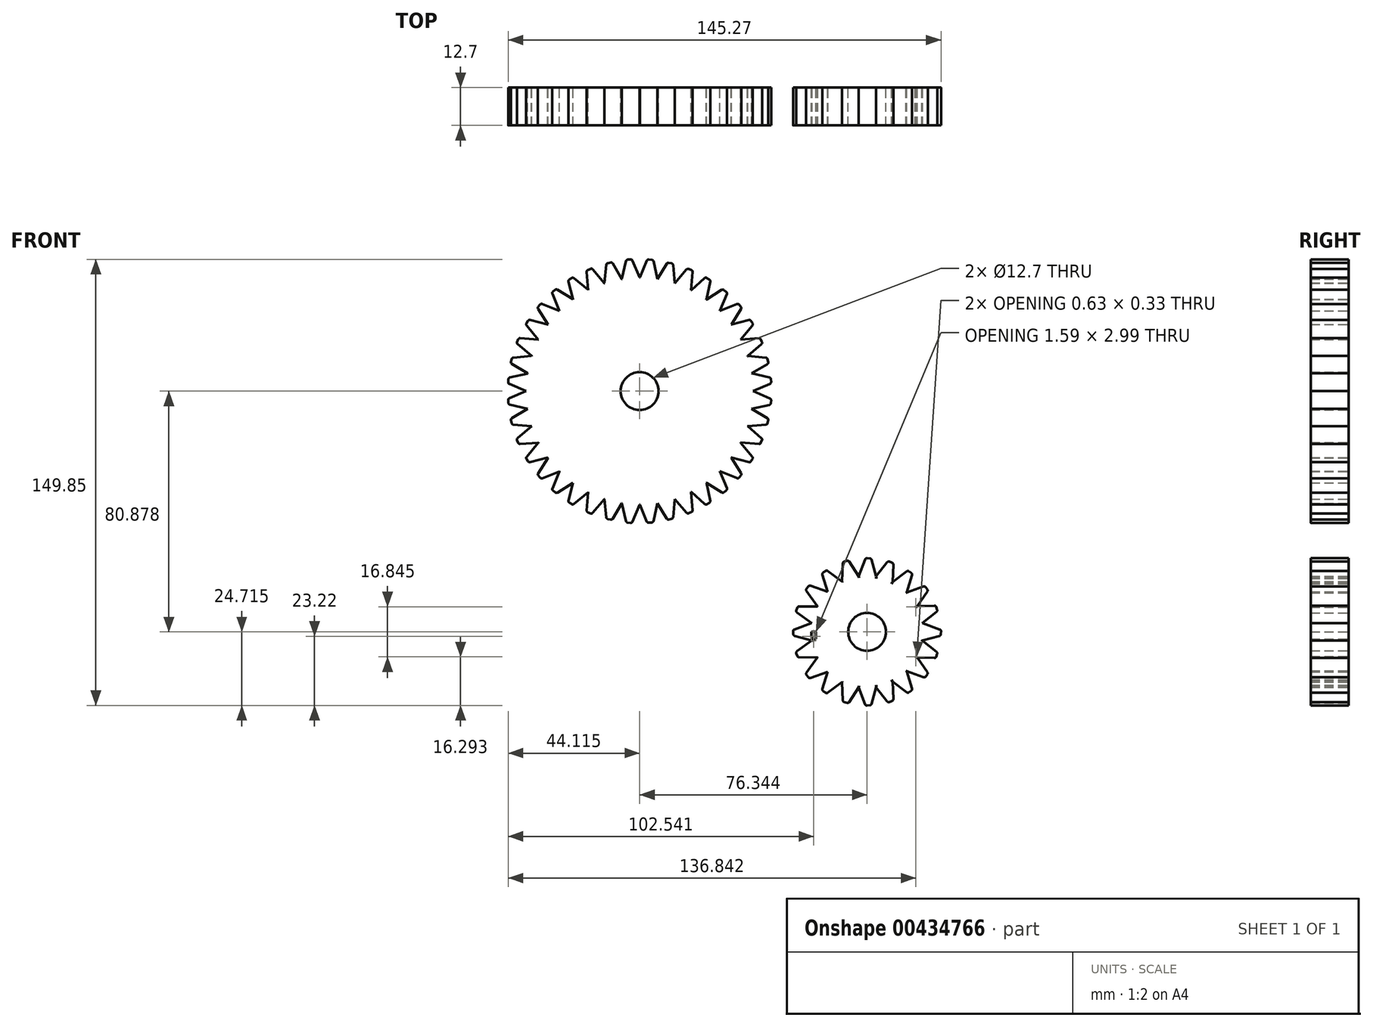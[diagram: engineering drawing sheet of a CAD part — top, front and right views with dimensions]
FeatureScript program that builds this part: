
annotation { "Feature Type Name" : "Feature", "Feature Type Description" : "" }
export const myFeature = defineFeature(function(context is Context, id is Id, definition is map)
    precondition{}
    {
        {
            var Q0;
            Q0=qCreatedBy(makeId("Front.planeOp"),FACE);
            var sketch = newSketch(context, id + "F0", { "sketchPlane" : qUnion([Q0])});
            skCircle(sketch, "E0", {"center": v(-35.87, 35.66) * mm, "radius": 38.1 * mm});
            skCircle(sketch, "E1", {"center": v(40.47, -45.22) * mm, "radius": 18.71 * mm});
            skCircle(sketch, "E2", {"center": v(-35.87, 35.66) * mm, "radius": 6.35 * mm});
            skCircle(sketch, "E3", {"center": v(40.47, -45.22) * mm, "radius": 6.35 * mm});
            skLineSegment(sketch, "E4", {"start": v(2.23, 35.66) * mm, "end": v(-73.97, 35.66) * mm, "construction": true});
            skLineSegment(sketch, "E5", {"start": v(-35.87, 73.76) * mm, "end": v(-35.87, -2.44) * mm, "construction": true});
            skLineSegment(sketch, "E6", {"start": v(-35.87, 35.66) * mm, "end": v(-41.83, 73.3) * mm, "construction": true});
            skLineSegment(sketch, "E7", {"start": v(-35.87, 35.66) * mm, "end": v(-47.65, 71.9) * mm, "construction": true});
            skLineSegment(sketch, "E8", {"start": v(-35.87, 35.66) * mm, "end": v(-53.17, 69.61) * mm, "construction": true});
            skLineSegment(sketch, "E9", {"start": v(-35.87, 35.66) * mm, "end": v(-58.27, 66.49) * mm, "construction": true});
            skLineSegment(sketch, "E10", {"start": v(-35.87, 35.66) * mm, "end": v(-62.82, 62.6) * mm, "construction": true});
            skLineSegment(sketch, "E11", {"start": v(-35.87, 35.66) * mm, "end": v(-66.7, 58.06) * mm, "construction": true});
            skLineSegment(sketch, "E12", {"start": v(-35.87, 35.66) * mm, "end": v(-69.82, 52.96) * mm, "construction": true});
            skLineSegment(sketch, "E13", {"start": v(-35.87, 35.66) * mm, "end": v(-72.1, 47.44) * mm, "construction": true});
            skLineSegment(sketch, "E14", {"start": v(-35.87, 35.66) * mm, "end": v(-73.5, 41.62) * mm, "construction": true});
            skLineSegment(sketch, "E15.MirrorCS", {"start": v(-35.87, 35.66) * mm, "end": v(1.76, 29.7) * mm, "construction": true});
            skLineSegment(sketch, "E16.MirrorCS", {"start": v(-35.87, 35.66) * mm, "end": v(0.36, 23.89) * mm, "construction": true});
            skLineSegment(sketch, "E17.MirrorCS", {"start": v(-35.87, 35.66) * mm, "end": v(-1.93, 18.37) * mm, "construction": true});
            skLineSegment(sketch, "E18.MirrorCS", {"start": v(-35.87, 35.66) * mm, "end": v(-5.05, 13.27) * mm, "construction": true});
            skLineSegment(sketch, "E19.MirrorCS", {"start": v(-35.87, 35.66) * mm, "end": v(-13.48, 4.84) * mm, "construction": true});
            skLineSegment(sketch, "E20.MirrorCS", {"start": v(-35.87, 35.66) * mm, "end": v(-18.58, 1.72) * mm, "construction": true});
            skLineSegment(sketch, "E21.MirrorCS", {"start": v(-35.87, 35.66) * mm, "end": v(-24.1, -0.57) * mm, "construction": true});
            skLineSegment(sketch, "E22", {"start": v(-35.87, 35.66) * mm, "end": v(-29.91, 73.3) * mm, "construction": true});
            skLineSegment(sketch, "E23", {"start": v(-35.87, 35.66) * mm, "end": v(-24.1, 71.9) * mm, "construction": true});
            skLineSegment(sketch, "E24", {"start": v(-35.87, 35.66) * mm, "end": v(-18.58, 69.61) * mm, "construction": true});
            skLineSegment(sketch, "E25", {"start": v(-35.87, 35.66) * mm, "end": v(-13.48, 66.49) * mm, "construction": true});
            skLineSegment(sketch, "E26", {"start": v(-35.87, 35.66) * mm, "end": v(-8.93, 62.6) * mm, "construction": true});
            skLineSegment(sketch, "E27", {"start": v(-35.87, 35.66) * mm, "end": v(-5.05, 58.06) * mm, "construction": true});
            skLineSegment(sketch, "E28", {"start": v(-35.87, 35.66) * mm, "end": v(-1.93, 52.96) * mm, "construction": true});
            skLineSegment(sketch, "E29", {"start": v(-35.87, 35.66) * mm, "end": v(0.36, 47.44) * mm, "construction": true});
            skLineSegment(sketch, "E30", {"start": v(-35.87, 35.66) * mm, "end": v(1.76, 41.62) * mm, "construction": true});
            skLineSegment(sketch, "E31", {"start": v(-35.87, 35.66) * mm, "end": v(-29.91, -1.97) * mm, "construction": true});
            skLineSegment(sketch, "E32", {"start": v(-35.87, 35.66) * mm, "end": v(-73.5, 29.7) * mm, "construction": true});
            skLineSegment(sketch, "E33", {"start": v(-35.87, 35.66) * mm, "end": v(-72.1, 23.89) * mm, "construction": true});
            skLineSegment(sketch, "E34", {"start": v(-35.87, 35.66) * mm, "end": v(-69.82, 18.37) * mm, "construction": true});
            skLineSegment(sketch, "E35", {"start": v(-35.87, 35.66) * mm, "end": v(-66.7, 13.27) * mm, "construction": true});
            skLineSegment(sketch, "E36", {"start": v(-35.87, 35.66) * mm, "end": v(-58.27, 4.84) * mm, "construction": true});
            skLineSegment(sketch, "E37", {"start": v(-35.87, 35.66) * mm, "end": v(-53.17, 1.72) * mm, "construction": true});
            skLineSegment(sketch, "E38", {"start": v(-35.87, 35.66) * mm, "end": v(-47.65, -0.57) * mm, "construction": true});
            skLineSegment(sketch, "E39", {"start": v(-35.87, 35.66) * mm, "end": v(-41.83, -1.97) * mm, "construction": true});
            skLineSegment(sketch, "E40", {"start": v(-35.87, 35.66) * mm, "end": v(-8.93, 8.72) * mm, "construction": true});
            skLineSegment(sketch, "E41", {"start": v(-35.87, 35.66) * mm, "end": v(-62.82, 8.72) * mm, "construction": true});
            skLineSegment(sketch, "E42", {"start": v(-41.82, 73.38) * mm, "end": v(-41.2, 72.13) * mm});
            skLineSegment(sketch, "E43", {"start": v(-41.2, 72.13) * mm, "end": v(-36.26, 72.56) * mm});
            skLineSegment(sketch, "E44", {"start": v(-36.26, 72.56) * mm, "end": v(-35.87, 73.9) * mm});
            skLineSegment(sketch, "E45", {"start": v(-35.87, 73.9) * mm, "end": v(-38.27, 79.55) * mm});
            skLineSegment(sketch, "E46", {"start": v(-38.89, 79.92) * mm, "end": v(-39.9, 79.83) * mm});
            skLineSegment(sketch, "E47", {"start": v(-40.44, 79.36) * mm, "end": v(-41.82, 73.38) * mm});
            skPoint(sketch, "E48.visualSharp", {"position": v(-40.34, 79.8) * mm});
            skArc(sketch, "E48.filletArc", {"start": v(-39.9, 79.83) * mm, "mid": v(-40.25, 79.69) * mm, "end": v(-40.44, 79.36) * mm});
            skPoint(sketch, "E49.visualSharp", {"position": v(-38.44, 79.96) * mm});
            skArc(sketch, "E49.filletArc", {"start": v(-38.27, 79.55) * mm, "mid": v(-38.52, 79.84) * mm, "end": v(-38.89, 79.92) * mm});
            skLineSegment(sketch, "E50", {"start": v(-35.82, 73.87) * mm, "end": v(-35.44, 72.53) * mm});
            skLineSegment(sketch, "E51", {"start": v(-35.44, 72.53) * mm, "end": v(-30.49, 72.1) * mm});
            skLineSegment(sketch, "E52", {"start": v(-30.49, 72.1) * mm, "end": v(-29.88, 73.35) * mm});
            skLineSegment(sketch, "E53", {"start": v(-29.88, 73.35) * mm, "end": v(-31.26, 79.33) * mm});
            skLineSegment(sketch, "E54", {"start": v(-31.8, 79.8) * mm, "end": v(-32.8, 79.9) * mm});
            skLineSegment(sketch, "E55", {"start": v(-33.42, 79.52) * mm, "end": v(-35.82, 73.87) * mm});
            skPoint(sketch, "E56.visualSharp", {"position": v(-33.25, 79.93) * mm});
            skArc(sketch, "E56.filletArc", {"start": v(-32.8, 79.9) * mm, "mid": v(-33.18, 79.8) * mm, "end": v(-33.42, 79.52) * mm});
            skPoint(sketch, "E57.visualSharp", {"position": v(-31.36, 79.76) * mm});
            skArc(sketch, "E57.filletArc", {"start": v(-31.26, 79.33) * mm, "mid": v(-31.45, 79.65) * mm, "end": v(-31.8, 79.8) * mm});
            skLineSegment(sketch, "E58", {"start": v(-29.92, 73.24) * mm, "end": v(-29.72, 71.85) * mm});
            skLineSegment(sketch, "E59", {"start": v(-29.72, 71.85) * mm, "end": v(-24.87, 70.75) * mm});
            skLineSegment(sketch, "E60", {"start": v(-24.87, 70.75) * mm, "end": v(-24.1, 71.92) * mm});
            skLineSegment(sketch, "E61", {"start": v(-24.1, 71.92) * mm, "end": v(-24.65, 78.03) * mm});
            skLineSegment(sketch, "E62", {"start": v(-25.12, 78.57) * mm, "end": v(-26.12, 78.8) * mm});
            skLineSegment(sketch, "E63", {"start": v(-26.77, 78.5) * mm, "end": v(-29.92, 73.24) * mm});
            skPoint(sketch, "E64.visualSharp", {"position": v(-26.55, 78.89) * mm});
            skArc(sketch, "E64.filletArc", {"start": v(-26.12, 78.8) * mm, "mid": v(-26.5, 78.76) * mm, "end": v(-26.77, 78.5) * mm});
            skPoint(sketch, "E65.visualSharp", {"position": v(-24.7, 78.47) * mm});
            skArc(sketch, "E65.filletArc", {"start": v(-24.65, 78.03) * mm, "mid": v(-24.8, 78.37) * mm, "end": v(-25.12, 78.57) * mm});
            skLineSegment(sketch, "E66", {"start": v(-47.66, 71.98) * mm, "end": v(-46.89, 70.82) * mm});
            skLineSegment(sketch, "E67", {"start": v(-46.89, 70.82) * mm, "end": v(-42.04, 71.88) * mm});
            skLineSegment(sketch, "E68", {"start": v(-42.04, 71.88) * mm, "end": v(-41.83, 73.27) * mm});
            skLineSegment(sketch, "E69", {"start": v(-41.83, 73.27) * mm, "end": v(-44.94, 78.56) * mm});
            skLineSegment(sketch, "E70", {"start": v(-45.6, 78.85) * mm, "end": v(-46.58, 78.63) * mm});
            skLineSegment(sketch, "E71", {"start": v(-47.06, 78.1) * mm, "end": v(-47.66, 71.98) * mm});
            skPoint(sketch, "E72.visualSharp", {"position": v(-47.02, 78.53) * mm});
            skArc(sketch, "E72.filletArc", {"start": v(-46.58, 78.63) * mm, "mid": v(-46.9, 78.44) * mm, "end": v(-47.06, 78.1) * mm});
            skPoint(sketch, "E73.visualSharp", {"position": v(-45.16, 78.94) * mm});
            skArc(sketch, "E73.filletArc", {"start": v(-44.94, 78.56) * mm, "mid": v(-45.22, 78.8) * mm, "end": v(-45.6, 78.85) * mm});
            skLineSegment(sketch, "E74", {"start": v(-53.16, 69.64) * mm, "end": v(-52.2, 68.62) * mm});
            skLineSegment(sketch, "E75", {"start": v(-52.2, 68.62) * mm, "end": v(-47.6, 70.5) * mm});
            skLineSegment(sketch, "E76", {"start": v(-47.6, 70.5) * mm, "end": v(-47.64, 71.9) * mm});
            skLineSegment(sketch, "E77", {"start": v(-47.64, 71.9) * mm, "end": v(-51.62, 76.58) * mm});
            skLineSegment(sketch, "E78", {"start": v(-52.31, 76.75) * mm, "end": v(-53.25, 76.37) * mm});
            skLineSegment(sketch, "E79", {"start": v(-53.63, 75.76) * mm, "end": v(-53.16, 69.64) * mm});
            skPoint(sketch, "E80.visualSharp", {"position": v(-53.66, 76.2) * mm});
            skArc(sketch, "E80.filletArc", {"start": v(-53.25, 76.37) * mm, "mid": v(-53.54, 76.12) * mm, "end": v(-53.63, 75.76) * mm});
            skPoint(sketch, "E81.visualSharp", {"position": v(-51.9, 76.92) * mm});
            skArc(sketch, "E81.filletArc", {"start": v(-51.62, 76.58) * mm, "mid": v(-51.94, 76.78) * mm, "end": v(-52.31, 76.75) * mm});
            skLineSegment(sketch, "E82", {"start": v(-58.26, 66.5) * mm, "end": v(-57.13, 65.66) * mm});
            skLineSegment(sketch, "E83", {"start": v(-57.13, 65.66) * mm, "end": v(-52.94, 68.33) * mm});
            skLineSegment(sketch, "E84", {"start": v(-52.94, 68.33) * mm, "end": v(-53.22, 69.7) * mm});
            skLineSegment(sketch, "E85", {"start": v(-53.22, 69.7) * mm, "end": v(-57.96, 73.6) * mm});
            skLineSegment(sketch, "E86", {"start": v(-58.67, 73.65) * mm, "end": v(-59.53, 73.1) * mm});
            skLineSegment(sketch, "E87", {"start": v(-59.8, 72.44) * mm, "end": v(-58.26, 66.5) * mm});
            skPoint(sketch, "E88.visualSharp", {"position": v(-59.9, 72.87) * mm});
            skArc(sketch, "E88.filletArc", {"start": v(-59.53, 73.1) * mm, "mid": v(-59.77, 72.81) * mm, "end": v(-59.8, 72.44) * mm});
            skPoint(sketch, "E89.visualSharp", {"position": v(-58.3, 73.89) * mm});
            skArc(sketch, "E89.filletArc", {"start": v(-57.96, 73.6) * mm, "mid": v(-58.3, 73.74) * mm, "end": v(-58.67, 73.65) * mm});
            skLineSegment(sketch, "E90", {"start": v(-62.86, 62.68) * mm, "end": v(-61.64, 62) * mm});
            skLineSegment(sketch, "E91", {"start": v(-61.64, 62) * mm, "end": v(-57.84, 65.2) * mm});
            skLineSegment(sketch, "E92", {"start": v(-57.84, 65.2) * mm, "end": v(-58.3, 66.51) * mm});
            skLineSegment(sketch, "E93", {"start": v(-58.3, 66.51) * mm, "end": v(-63.5, 69.77) * mm});
            skLineSegment(sketch, "E94", {"start": v(-64.21, 69.72) * mm, "end": v(-64.99, 69.06) * mm});
            skLineSegment(sketch, "E95", {"start": v(-65.16, 68.37) * mm, "end": v(-62.86, 62.68) * mm});
            skPoint(sketch, "E96.visualSharp", {"position": v(-65.33, 68.78) * mm});
            skArc(sketch, "E96.filletArc", {"start": v(-64.99, 69.06) * mm, "mid": v(-65.19, 68.74) * mm, "end": v(-65.16, 68.37) * mm});
            skPoint(sketch, "E97.visualSharp", {"position": v(-63.87, 70) * mm});
            skArc(sketch, "E97.filletArc", {"start": v(-63.5, 69.77) * mm, "mid": v(-63.86, 69.86) * mm, "end": v(-64.21, 69.72) * mm});
            skLineSegment(sketch, "E98", {"start": v(-66.7, 58.07) * mm, "end": v(-65.37, 57.62) * mm});
            skLineSegment(sketch, "E99", {"start": v(-65.37, 57.62) * mm, "end": v(-62.18, 61.42) * mm});
            skLineSegment(sketch, "E100", {"start": v(-62.18, 61.42) * mm, "end": v(-62.85, 62.64) * mm});
            skLineSegment(sketch, "E101", {"start": v(-62.85, 62.64) * mm, "end": v(-68.54, 64.94) * mm});
            skLineSegment(sketch, "E102", {"start": v(-69.24, 64.77) * mm, "end": v(-69.9, 64) * mm});
            skLineSegment(sketch, "E103", {"start": v(-69.94, 63.28) * mm, "end": v(-66.7, 58.07) * mm});
            skPoint(sketch, "E104.visualSharp", {"position": v(-70.18, 63.65) * mm});
            skArc(sketch, "E104.filletArc", {"start": v(-69.9, 64) * mm, "mid": v(-70.03, 63.64) * mm, "end": v(-69.94, 63.28) * mm});
            skPoint(sketch, "E105.visualSharp", {"position": v(-68.96, 65.1) * mm});
            skArc(sketch, "E105.filletArc", {"start": v(-68.54, 64.94) * mm, "mid": v(-68.92, 64.97) * mm, "end": v(-69.24, 64.77) * mm});
            skLineSegment(sketch, "E106", {"start": v(-69.88, 52.98) * mm, "end": v(-68.51, 52.7) * mm});
            skLineSegment(sketch, "E107", {"start": v(-68.51, 52.7) * mm, "end": v(-65.85, 56.9) * mm});
            skLineSegment(sketch, "E108", {"start": v(-65.85, 56.9) * mm, "end": v(-66.69, 58.03) * mm});
            skLineSegment(sketch, "E109", {"start": v(-66.69, 58.03) * mm, "end": v(-72.63, 59.55) * mm});
            skLineSegment(sketch, "E110", {"start": v(-73.3, 59.28) * mm, "end": v(-73.84, 58.42) * mm});
            skLineSegment(sketch, "E111", {"start": v(-73.8, 57.7) * mm, "end": v(-69.88, 52.98) * mm});
            skPoint(sketch, "E112.visualSharp", {"position": v(-74.08, 58.05) * mm});
            skArc(sketch, "E112.filletArc", {"start": v(-73.84, 58.42) * mm, "mid": v(-73.94, 58.06) * mm, "end": v(-73.8, 57.7) * mm});
            skPoint(sketch, "E113.visualSharp", {"position": v(-73.06, 59.66) * mm});
            skArc(sketch, "E113.filletArc", {"start": v(-72.63, 59.55) * mm, "mid": v(-73, 59.52) * mm, "end": v(-73.3, 59.28) * mm});
            skLineSegment(sketch, "E114", {"start": v(-72.14, 47.45) * mm, "end": v(-70.74, 47.42) * mm});
            skLineSegment(sketch, "E115", {"start": v(-70.74, 47.42) * mm, "end": v(-68.85, 52.01) * mm});
            skLineSegment(sketch, "E116", {"start": v(-68.85, 52.01) * mm, "end": v(-69.87, 52.97) * mm});
            skLineSegment(sketch, "E117", {"start": v(-69.87, 52.97) * mm, "end": v(-75.99, 53.44) * mm});
            skLineSegment(sketch, "E118", {"start": v(-76.6, 53.06) * mm, "end": v(-76.99, 52.12) * mm});
            skLineSegment(sketch, "E119", {"start": v(-76.82, 51.43) * mm, "end": v(-72.14, 47.45) * mm});
            skPoint(sketch, "E120.visualSharp", {"position": v(-77.15, 51.71) * mm});
            skArc(sketch, "E120.filletArc", {"start": v(-76.99, 52.12) * mm, "mid": v(-77.01, 51.75) * mm, "end": v(-76.82, 51.43) * mm});
            skPoint(sketch, "E121.visualSharp", {"position": v(-76.43, 53.47) * mm});
            skArc(sketch, "E121.filletArc", {"start": v(-75.99, 53.44) * mm, "mid": v(-76.35, 53.35) * mm, "end": v(-76.6, 53.06) * mm});
            skLineSegment(sketch, "E122", {"start": v(-73.5, 41.64) * mm, "end": v(-72.12, 41.84) * mm});
            skLineSegment(sketch, "E123", {"start": v(-72.12, 41.84) * mm, "end": v(-71, 46.68) * mm});
            skLineSegment(sketch, "E124", {"start": v(-71, 46.68) * mm, "end": v(-72.16, 47.46) * mm});
            skLineSegment(sketch, "E125", {"start": v(-72.16, 47.46) * mm, "end": v(-78.27, 46.92) * mm});
            skLineSegment(sketch, "E126", {"start": v(-78.81, 46.45) * mm, "end": v(-79.04, 45.46) * mm});
            skLineSegment(sketch, "E127", {"start": v(-78.76, 44.8) * mm, "end": v(-73.5, 41.64) * mm});
            skPoint(sketch, "E128.visualSharp", {"position": v(-79.14, 45.03) * mm});
            skArc(sketch, "E128.filletArc", {"start": v(-79.04, 45.46) * mm, "mid": v(-79, 45.09) * mm, "end": v(-78.76, 44.8) * mm});
            skPoint(sketch, "E129.visualSharp", {"position": v(-78.71, 46.89) * mm});
            skArc(sketch, "E129.filletArc", {"start": v(-78.27, 46.92) * mm, "mid": v(-78.62, 46.78) * mm, "end": v(-78.81, 46.45) * mm});
            skLineSegment(sketch, "E130", {"start": v(-73.97, 35.65) * mm, "end": v(-72.63, 36.04) * mm});
            skLineSegment(sketch, "E131", {"start": v(-72.63, 36.04) * mm, "end": v(-72.2, 40.99) * mm});
            skLineSegment(sketch, "E132", {"start": v(-72.2, 40.99) * mm, "end": v(-73.45, 41.6) * mm});
            skLineSegment(sketch, "E133", {"start": v(-73.45, 41.6) * mm, "end": v(-79.43, 40.22) * mm});
            skLineSegment(sketch, "E134", {"start": v(-79.9, 39.68) * mm, "end": v(-80, 38.66) * mm});
            skLineSegment(sketch, "E135", {"start": v(-79.62, 38.05) * mm, "end": v(-73.97, 35.65) * mm});
            skPoint(sketch, "E136.visualSharp", {"position": v(-80.03, 38.22) * mm});
            skArc(sketch, "E136.filletArc", {"start": v(-80, 38.66) * mm, "mid": v(-79.9, 38.3) * mm, "end": v(-79.62, 38.05) * mm});
            skPoint(sketch, "E137.visualSharp", {"position": v(-79.86, 40.12) * mm});
            skArc(sketch, "E137.filletArc", {"start": v(-79.43, 40.22) * mm, "mid": v(-79.75, 40.02) * mm, "end": v(-79.9, 39.68) * mm});
            skLineSegment(sketch, "E138", {"start": v(-24.1, 71.9) * mm, "end": v(-24.15, 70.5) * mm});
            skLineSegment(sketch, "E139", {"start": v(-24.15, 70.5) * mm, "end": v(-19.57, 68.57) * mm});
            skLineSegment(sketch, "E140", {"start": v(-19.57, 68.57) * mm, "end": v(-18.6, 69.58) * mm});
            skLineSegment(sketch, "E141", {"start": v(-18.6, 69.58) * mm, "end": v(-18.08, 75.7) * mm});
            skLineSegment(sketch, "E142", {"start": v(-18.46, 76.3) * mm, "end": v(-19.4, 76.7) * mm});
            skLineSegment(sketch, "E143", {"start": v(-20.1, 76.54) * mm, "end": v(-24.1, 71.9) * mm});
            skPoint(sketch, "E144.visualSharp", {"position": v(-19.8, 76.87) * mm});
            skArc(sketch, "E144.filletArc", {"start": v(-19.4, 76.7) * mm, "mid": v(-19.77, 76.73) * mm, "end": v(-20.1, 76.54) * mm});
            skPoint(sketch, "E145.visualSharp", {"position": v(-18.05, 76.14) * mm});
            skArc(sketch, "E145.filletArc", {"start": v(-18.08, 75.7) * mm, "mid": v(-18.17, 76.06) * mm, "end": v(-18.46, 76.3) * mm});
            skLineSegment(sketch, "E146", {"start": v(-18.64, 69.5) * mm, "end": v(-18.85, 68.12) * mm});
            skLineSegment(sketch, "E147", {"start": v(-18.85, 68.12) * mm, "end": v(-14.55, 65.64) * mm});
            skLineSegment(sketch, "E148", {"start": v(-14.55, 65.64) * mm, "end": v(-13.46, 66.52) * mm});
            skLineSegment(sketch, "E149", {"start": v(-13.46, 66.52) * mm, "end": v(-12.2, 72.53) * mm});
            skLineSegment(sketch, "E150", {"start": v(-12.5, 73.18) * mm, "end": v(-13.37, 73.69) * mm});
            skLineSegment(sketch, "E151", {"start": v(-14.08, 73.61) * mm, "end": v(-18.64, 69.5) * mm});
            skPoint(sketch, "E152.visualSharp", {"position": v(-13.76, 73.9) * mm});
            skArc(sketch, "E152.filletArc", {"start": v(-13.37, 73.69) * mm, "mid": v(-13.74, 73.77) * mm, "end": v(-14.08, 73.61) * mm});
            skPoint(sketch, "E153.visualSharp", {"position": v(-12.1, 72.96) * mm});
            skArc(sketch, "E153.filletArc", {"start": v(-12.2, 72.53) * mm, "mid": v(-12.24, 72.9) * mm, "end": v(-12.5, 73.18) * mm});
            skLineSegment(sketch, "E154", {"start": v(-13.48, 66.44) * mm, "end": v(-13.94, 65.12) * mm});
            skLineSegment(sketch, "E155", {"start": v(-13.94, 65.12) * mm, "end": v(-10.13, 61.93) * mm});
            skLineSegment(sketch, "E156", {"start": v(-10.13, 61.93) * mm, "end": v(-8.9, 62.6) * mm});
            skLineSegment(sketch, "E157", {"start": v(-8.9, 62.6) * mm, "end": v(-6.61, 68.3) * mm});
            skLineSegment(sketch, "E158", {"start": v(-6.78, 68.99) * mm, "end": v(-7.56, 69.64) * mm});
            skLineSegment(sketch, "E159", {"start": v(-8.28, 69.7) * mm, "end": v(-13.48, 66.44) * mm});
            skPoint(sketch, "E160.visualSharp", {"position": v(-7.9, 69.93) * mm});
            skArc(sketch, "E160.filletArc", {"start": v(-7.56, 69.64) * mm, "mid": v(-7.91, 69.78) * mm, "end": v(-8.28, 69.7) * mm});
            skPoint(sketch, "E161.visualSharp", {"position": v(-6.44, 68.7) * mm});
            skArc(sketch, "E161.filletArc", {"start": v(-6.61, 68.3) * mm, "mid": v(-6.58, 68.67) * mm, "end": v(-6.78, 68.99) * mm});
            skLineSegment(sketch, "E162", {"start": v(-8.92, 62.6) * mm, "end": v(-9.6, 61.38) * mm});
            skLineSegment(sketch, "E163", {"start": v(-9.6, 61.38) * mm, "end": v(-6.4, 57.57) * mm});
            skLineSegment(sketch, "E164", {"start": v(-6.4, 57.57) * mm, "end": v(-5.08, 58.03) * mm});
            skLineSegment(sketch, "E165", {"start": v(-5.08, 58.03) * mm, "end": v(-1.83, 63.23) * mm});
            skLineSegment(sketch, "E166", {"start": v(-1.88, 63.95) * mm, "end": v(-2.53, 64.73) * mm});
            skLineSegment(sketch, "E167", {"start": v(-3.23, 64.9) * mm, "end": v(-8.92, 62.6) * mm});
            skPoint(sketch, "E168.visualSharp", {"position": v(-2.82, 65.07) * mm});
            skArc(sketch, "E168.filletArc", {"start": v(-2.53, 64.73) * mm, "mid": v(-2.85, 64.93) * mm, "end": v(-3.23, 64.9) * mm});
            skPoint(sketch, "E169.visualSharp", {"position": v(-1.6, 63.61) * mm});
            skArc(sketch, "E169.filletArc", {"start": v(-1.83, 63.23) * mm, "mid": v(-1.74, 63.6) * mm, "end": v(-1.88, 63.95) * mm});
            skLineSegment(sketch, "E170", {"start": v(-5.11, 58.03) * mm, "end": v(-5.95, 56.9) * mm});
            skLineSegment(sketch, "E171", {"start": v(-5.95, 56.9) * mm, "end": v(-3.3, 52.7) * mm});
            skLineSegment(sketch, "E172", {"start": v(-3.3, 52.7) * mm, "end": v(-1.92, 52.98) * mm});
            skLineSegment(sketch, "E173", {"start": v(-1.92, 52.98) * mm, "end": v(2, 57.7) * mm});
            skLineSegment(sketch, "E174", {"start": v(2.04, 58.42) * mm, "end": v(1.5, 59.28) * mm});
            skLineSegment(sketch, "E175", {"start": v(0.83, 59.54) * mm, "end": v(-5.11, 58.03) * mm});
            skPoint(sketch, "E176.visualSharp", {"position": v(1.26, 59.65) * mm});
            skArc(sketch, "E176.filletArc", {"start": v(1.5, 59.28) * mm, "mid": v(1.21, 59.52) * mm, "end": v(0.83, 59.54) * mm});
            skPoint(sketch, "E177.visualSharp", {"position": v(2.28, 58.04) * mm});
            skArc(sketch, "E177.filletArc", {"start": v(2, 57.7) * mm, "mid": v(2.14, 58.05) * mm, "end": v(2.04, 58.42) * mm});
            skLineSegment(sketch, "E178", {"start": v(-1.94, 52.95) * mm, "end": v(-2.95, 51.99) * mm});
            skLineSegment(sketch, "E179", {"start": v(-2.95, 51.99) * mm, "end": v(-1.02, 47.4) * mm});
            skLineSegment(sketch, "E180", {"start": v(-1.02, 47.4) * mm, "end": v(0.37, 47.45) * mm});
            skLineSegment(sketch, "E181", {"start": v(0.37, 47.45) * mm, "end": v(5.02, 51.46) * mm});
            skLineSegment(sketch, "E182", {"start": v(5.18, 52.15) * mm, "end": v(4.8, 53.1) * mm});
            skLineSegment(sketch, "E183", {"start": v(4.18, 53.46) * mm, "end": v(-1.94, 52.95) * mm});
            skPoint(sketch, "E184.visualSharp", {"position": v(4.62, 53.5) * mm});
            skArc(sketch, "E184.filletArc", {"start": v(4.8, 53.1) * mm, "mid": v(4.54, 53.38) * mm, "end": v(4.18, 53.46) * mm});
            skPoint(sketch, "E185.visualSharp", {"position": v(5.36, 51.75) * mm});
            skArc(sketch, "E185.filletArc", {"start": v(5.02, 51.46) * mm, "mid": v(5.22, 51.78) * mm, "end": v(5.18, 52.15) * mm});
            skLineSegment(sketch, "E186", {"start": v(0.43, 47.45) * mm, "end": v(-0.73, 46.67) * mm});
            skLineSegment(sketch, "E187", {"start": v(-0.73, 46.67) * mm, "end": v(0.36, 41.83) * mm});
            skLineSegment(sketch, "E188", {"start": v(0.36, 41.83) * mm, "end": v(1.74, 41.63) * mm});
            skLineSegment(sketch, "E189", {"start": v(1.74, 41.63) * mm, "end": v(7.02, 44.76) * mm});
            skLineSegment(sketch, "E190", {"start": v(7.3, 45.42) * mm, "end": v(7.08, 46.41) * mm});
            skLineSegment(sketch, "E191", {"start": v(6.54, 46.88) * mm, "end": v(0.43, 47.45) * mm});
            skPoint(sketch, "E192.visualSharp", {"position": v(6.98, 46.84) * mm});
            skArc(sketch, "E192.filletArc", {"start": v(7.08, 46.41) * mm, "mid": v(6.89, 46.74) * mm, "end": v(6.54, 46.88) * mm});
            skPoint(sketch, "E193.visualSharp", {"position": v(7.4, 44.99) * mm});
            skArc(sketch, "E193.filletArc", {"start": v(7.02, 44.76) * mm, "mid": v(7.27, 45.05) * mm, "end": v(7.3, 45.42) * mm});
            skLineSegment(sketch, "E194", {"start": v(1.68, 41.62) * mm, "end": v(0.43, 41) * mm});
            skLineSegment(sketch, "E195", {"start": v(0.43, 41) * mm, "end": v(0.9, 36.06) * mm});
            skLineSegment(sketch, "E196", {"start": v(0.9, 36.06) * mm, "end": v(2.24, 35.68) * mm});
            skLineSegment(sketch, "E197", {"start": v(2.24, 35.68) * mm, "end": v(7.88, 38.12) * mm});
            skLineSegment(sketch, "E198", {"start": v(8.24, 38.74) * mm, "end": v(8.15, 39.75) * mm});
            skLineSegment(sketch, "E199", {"start": v(7.67, 40.28) * mm, "end": v(1.68, 41.62) * mm});
            skPoint(sketch, "E200.visualSharp", {"position": v(8.1, 40.19) * mm});
            skArc(sketch, "E200.filletArc", {"start": v(8.15, 39.75) * mm, "mid": v(8, 40.1) * mm, "end": v(7.67, 40.28) * mm});
            skPoint(sketch, "E201.visualSharp", {"position": v(8.28, 38.3) * mm});
            skArc(sketch, "E201.filletArc", {"start": v(7.88, 38.12) * mm, "mid": v(8.16, 38.37) * mm, "end": v(8.24, 38.74) * mm});
            skLineSegment(sketch, "E202.MirrorCS", {"start": v(-73.45, 29.73) * mm, "end": v(-79.43, 31.1) * mm});
            skLineSegment(sketch, "E203.MirrorCS", {"start": v(-79.62, 33.28) * mm, "end": v(-73.97, 35.67) * mm});
            skLineSegment(sketch, "E204.MirrorCS", {"start": v(-79.9, 31.65) * mm, "end": v(-80, 32.66) * mm});
            skLineSegment(sketch, "E205.MirrorCS", {"start": v(-73.97, 35.67) * mm, "end": v(-72.63, 35.29) * mm});
            skLineSegment(sketch, "E206.MirrorCS", {"start": v(-72.63, 35.29) * mm, "end": v(-72.2, 30.34) * mm});
            skLineSegment(sketch, "E207.MirrorCS", {"start": v(-72.2, 30.34) * mm, "end": v(-73.45, 29.73) * mm});
            skArc(sketch, "E208.MirrorCS", {"start": v(-79.43, 31.1) * mm, "mid": v(-79.75, 31.3) * mm, "end": v(-79.9, 31.65) * mm});
            skArc(sketch, "E209.MirrorCS", {"start": v(-80, 32.66) * mm, "mid": v(-79.9, 33.03) * mm, "end": v(-79.62, 33.28) * mm});
            skLineSegment(sketch, "E210.MirrorCS", {"start": v(-78.76, 26.52) * mm, "end": v(-73.5, 29.68) * mm});
            skLineSegment(sketch, "E211.MirrorCS", {"start": v(-72.12, 29.49) * mm, "end": v(-71, 24.65) * mm});
            skLineSegment(sketch, "E212.MirrorCS", {"start": v(-73.5, 29.68) * mm, "end": v(-72.12, 29.49) * mm});
            skLineSegment(sketch, "E213.MirrorCS", {"start": v(-71, 24.65) * mm, "end": v(-72.16, 23.87) * mm});
            skLineSegment(sketch, "E214.MirrorCS", {"start": v(-72.16, 23.87) * mm, "end": v(-78.27, 24.4) * mm});
            skArc(sketch, "E215.MirrorCS", {"start": v(-78.27, 24.4) * mm, "mid": v(-78.62, 24.55) * mm, "end": v(-78.81, 24.87) * mm});
            skLineSegment(sketch, "E216.MirrorCS", {"start": v(-78.81, 24.87) * mm, "end": v(-79.04, 25.86) * mm});
            skArc(sketch, "E217.MirrorCS", {"start": v(-79.04, 25.86) * mm, "mid": v(-79, 26.24) * mm, "end": v(-78.76, 26.52) * mm});
            skArc(sketch, "E218.MirrorCS", {"start": v(-75.99, 17.89) * mm, "mid": v(-76.35, 17.98) * mm, "end": v(-76.6, 18.26) * mm});
            skLineSegment(sketch, "E219.MirrorCS", {"start": v(-76.6, 18.26) * mm, "end": v(-76.99, 19.2) * mm});
            skArc(sketch, "E220.MirrorCS", {"start": v(-76.99, 19.2) * mm, "mid": v(-77.01, 19.58) * mm, "end": v(-76.82, 19.9) * mm});
            skLineSegment(sketch, "E221.MirrorCS", {"start": v(-76.82, 19.9) * mm, "end": v(-72.14, 23.88) * mm});
            skLineSegment(sketch, "E222.MirrorCS", {"start": v(-72.14, 23.88) * mm, "end": v(-70.74, 23.9) * mm});
            skLineSegment(sketch, "E223.MirrorCS", {"start": v(-70.74, 23.9) * mm, "end": v(-68.85, 19.31) * mm});
            skLineSegment(sketch, "E224.MirrorCS", {"start": v(-68.85, 19.31) * mm, "end": v(-69.87, 18.36) * mm});
            skLineSegment(sketch, "E225.MirrorCS", {"start": v(-69.87, 18.36) * mm, "end": v(-75.99, 17.89) * mm});
            skLineSegment(sketch, "E226.MirrorCS", {"start": v(-66.69, 13.3) * mm, "end": v(-72.63, 11.78) * mm});
            skArc(sketch, "E227.MirrorCS", {"start": v(-72.63, 11.78) * mm, "mid": v(-73, 11.8) * mm, "end": v(-73.3, 12.04) * mm});
            skLineSegment(sketch, "E228.MirrorCS", {"start": v(-73.3, 12.04) * mm, "end": v(-73.84, 12.9) * mm});
            skArc(sketch, "E229.MirrorCS", {"start": v(-73.84, 12.9) * mm, "mid": v(-73.94, 13.27) * mm, "end": v(-73.8, 13.62) * mm});
            skLineSegment(sketch, "E230.MirrorCS", {"start": v(-73.8, 13.62) * mm, "end": v(-69.88, 18.34) * mm});
            skLineSegment(sketch, "E231.MirrorCS", {"start": v(-69.88, 18.34) * mm, "end": v(-68.51, 18.62) * mm});
            skLineSegment(sketch, "E232.MirrorCS", {"start": v(-68.51, 18.62) * mm, "end": v(-65.85, 14.42) * mm});
            skLineSegment(sketch, "E233.MirrorCS", {"start": v(-65.85, 14.42) * mm, "end": v(-66.69, 13.3) * mm});
            skArc(sketch, "E234.MirrorCS", {"start": v(-68.54, 6.38) * mm, "mid": v(-68.92, 6.36) * mm, "end": v(-69.24, 6.56) * mm});
            skLineSegment(sketch, "E235.MirrorCS", {"start": v(-69.24, 6.56) * mm, "end": v(-69.9, 7.34) * mm});
            skArc(sketch, "E236.MirrorCS", {"start": v(-69.9, 7.34) * mm, "mid": v(-70.03, 7.68) * mm, "end": v(-69.94, 8.05) * mm});
            skLineSegment(sketch, "E237.MirrorCS", {"start": v(-69.94, 8.05) * mm, "end": v(-66.7, 13.26) * mm});
            skLineSegment(sketch, "E238.MirrorCS", {"start": v(-66.7, 13.26) * mm, "end": v(-65.37, 13.71) * mm});
            skLineSegment(sketch, "E239.MirrorCS", {"start": v(-65.37, 13.71) * mm, "end": v(-62.18, 9.9) * mm});
            skLineSegment(sketch, "E240.MirrorCS", {"start": v(-62.18, 9.9) * mm, "end": v(-62.85, 8.68) * mm});
            skLineSegment(sketch, "E241.MirrorCS", {"start": v(-62.85, 8.68) * mm, "end": v(-68.54, 6.38) * mm});
            skLineSegment(sketch, "E242.MirrorCS", {"start": v(-58.3, 4.81) * mm, "end": v(-63.5, 1.56) * mm});
            skArc(sketch, "E243.MirrorCS", {"start": v(-63.5, 1.56) * mm, "mid": v(-63.86, 1.47) * mm, "end": v(-64.21, 1.6) * mm});
            skLineSegment(sketch, "E244.MirrorCS", {"start": v(-64.21, 1.6) * mm, "end": v(-64.99, 2.26) * mm});
            skArc(sketch, "E245.MirrorCS", {"start": v(-64.99, 2.26) * mm, "mid": v(-65.19, 2.58) * mm, "end": v(-65.16, 2.96) * mm});
            skLineSegment(sketch, "E246.MirrorCS", {"start": v(-65.16, 2.96) * mm, "end": v(-62.86, 8.65) * mm});
            skLineSegment(sketch, "E247.MirrorCS", {"start": v(-62.86, 8.65) * mm, "end": v(-61.64, 9.33) * mm});
            skLineSegment(sketch, "E248.MirrorCS", {"start": v(-61.64, 9.33) * mm, "end": v(-57.84, 6.13) * mm});
            skLineSegment(sketch, "E249.MirrorCS", {"start": v(-57.84, 6.13) * mm, "end": v(-58.3, 4.81) * mm});
            skLineSegment(sketch, "E250.MirrorCS", {"start": v(-53.22, 1.63) * mm, "end": v(-57.96, -2.28) * mm});
            skArc(sketch, "E251.MirrorCS", {"start": v(-57.96, -2.28) * mm, "mid": v(-58.3, -2.42) * mm, "end": v(-58.67, -2.32) * mm});
            skLineSegment(sketch, "E252.MirrorCS", {"start": v(-58.67, -2.32) * mm, "end": v(-59.53, -1.78) * mm});
            skArc(sketch, "E253.MirrorCS", {"start": v(-59.53, -1.78) * mm, "mid": v(-59.77, -1.49) * mm, "end": v(-59.8, -1.11) * mm});
            skLineSegment(sketch, "E254.MirrorCS", {"start": v(-59.8, -1.11) * mm, "end": v(-58.26, 4.83) * mm});
            skLineSegment(sketch, "E255.MirrorCS", {"start": v(-58.26, 4.83) * mm, "end": v(-57.13, 5.66) * mm});
            skLineSegment(sketch, "E256.MirrorCS", {"start": v(-57.13, 5.66) * mm, "end": v(-52.94, 3) * mm});
            skLineSegment(sketch, "E257.MirrorCS", {"start": v(-52.94, 3) * mm, "end": v(-53.22, 1.63) * mm});
            skLineSegment(sketch, "E258.MirrorCS", {"start": v(-52.31, -5.43) * mm, "end": v(-53.25, -5.04) * mm});
            skArc(sketch, "E259.MirrorCS", {"start": v(-51.62, -5.26) * mm, "mid": v(-51.94, -5.46) * mm, "end": v(-52.31, -5.43) * mm});
            skArc(sketch, "E260.MirrorCS", {"start": v(-53.25, -5.04) * mm, "mid": v(-53.54, -4.8) * mm, "end": v(-53.63, -4.43) * mm});
            skLineSegment(sketch, "E261.MirrorCS", {"start": v(-53.63, -4.43) * mm, "end": v(-53.16, 1.69) * mm});
            skLineSegment(sketch, "E262.MirrorCS", {"start": v(-53.16, 1.69) * mm, "end": v(-52.2, 2.7) * mm});
            skLineSegment(sketch, "E263.MirrorCS", {"start": v(-52.2, 2.7) * mm, "end": v(-47.6, 0.82) * mm});
            skLineSegment(sketch, "E264.MirrorCS", {"start": v(-47.6, 0.82) * mm, "end": v(-47.64, -0.58) * mm});
            skLineSegment(sketch, "E265.MirrorCS", {"start": v(-47.64, -0.58) * mm, "end": v(-51.62, -5.26) * mm});
            skLineSegment(sketch, "E266.MirrorCS", {"start": v(-45.6, -7.52) * mm, "end": v(-46.58, -7.3) * mm});
            skArc(sketch, "E267.MirrorCS", {"start": v(-46.58, -7.3) * mm, "mid": v(-46.9, -7.11) * mm, "end": v(-47.06, -6.77) * mm});
            skLineSegment(sketch, "E268.MirrorCS", {"start": v(-47.06, -6.77) * mm, "end": v(-47.66, -0.66) * mm});
            skLineSegment(sketch, "E269.MirrorCS", {"start": v(-47.66, -0.66) * mm, "end": v(-46.89, 0.5) * mm});
            skLineSegment(sketch, "E270.MirrorCS", {"start": v(-46.89, 0.5) * mm, "end": v(-42.04, -0.56) * mm});
            skLineSegment(sketch, "E271.MirrorCS", {"start": v(-42.04, -0.56) * mm, "end": v(-41.83, -1.94) * mm});
            skLineSegment(sketch, "E272.MirrorCS", {"start": v(-41.83, -1.94) * mm, "end": v(-44.94, -7.23) * mm});
            skArc(sketch, "E273.MirrorCS", {"start": v(-44.94, -7.23) * mm, "mid": v(-45.22, -7.48) * mm, "end": v(-45.6, -7.52) * mm});
            skLineSegment(sketch, "E274.MirrorCS", {"start": v(-38.89, -8.6) * mm, "end": v(-39.9, -8.5) * mm});
            skArc(sketch, "E275.MirrorCS", {"start": v(-39.9, -8.5) * mm, "mid": v(-40.25, -8.36) * mm, "end": v(-40.44, -8.04) * mm});
            skLineSegment(sketch, "E276.MirrorCS", {"start": v(-40.44, -8.04) * mm, "end": v(-41.82, -2.06) * mm});
            skLineSegment(sketch, "E277.MirrorCS", {"start": v(-41.82, -2.06) * mm, "end": v(-41.2, -0.8) * mm});
            skLineSegment(sketch, "E278.MirrorCS", {"start": v(-41.2, -0.8) * mm, "end": v(-36.26, -1.23) * mm});
            skLineSegment(sketch, "E279.MirrorCS", {"start": v(-36.26, -1.23) * mm, "end": v(-35.87, -2.58) * mm});
            skLineSegment(sketch, "E280.MirrorCS", {"start": v(-35.87, -2.58) * mm, "end": v(-38.27, -8.23) * mm});
            skArc(sketch, "E281.MirrorCS", {"start": v(-38.27, -8.23) * mm, "mid": v(-38.52, -8.51) * mm, "end": v(-38.89, -8.6) * mm});
            skLineSegment(sketch, "E282.MirrorCS", {"start": v(-33.42, -8.2) * mm, "end": v(-35.82, -2.55) * mm});
            skArc(sketch, "E283.MirrorCS", {"start": v(-32.8, -8.56) * mm, "mid": v(-33.18, -8.48) * mm, "end": v(-33.42, -8.2) * mm});
            skLineSegment(sketch, "E284.MirrorCS", {"start": v(-31.8, -8.48) * mm, "end": v(-32.8, -8.56) * mm});
            skArc(sketch, "E285.MirrorCS", {"start": v(-31.26, -8) * mm, "mid": v(-31.45, -8.33) * mm, "end": v(-31.8, -8.48) * mm});
            skLineSegment(sketch, "E286.MirrorCS", {"start": v(-29.88, -2.03) * mm, "end": v(-31.26, -8) * mm});
            skLineSegment(sketch, "E287.MirrorCS", {"start": v(-30.49, -0.77) * mm, "end": v(-29.88, -2.03) * mm});
            skLineSegment(sketch, "E288.MirrorCS", {"start": v(-35.44, -1.2) * mm, "end": v(-30.49, -0.77) * mm});
            skLineSegment(sketch, "E289.MirrorCS", {"start": v(-35.82, -2.55) * mm, "end": v(-35.44, -1.2) * mm});
            skLineSegment(sketch, "E290.MirrorCS", {"start": v(-26.77, -7.18) * mm, "end": v(-29.92, -1.91) * mm});
            skLineSegment(sketch, "E291.MirrorCS", {"start": v(-29.92, -1.91) * mm, "end": v(-29.72, -0.53) * mm});
            skLineSegment(sketch, "E292.MirrorCS", {"start": v(-29.72, -0.53) * mm, "end": v(-24.87, 0.57) * mm});
            skLineSegment(sketch, "E293.MirrorCS", {"start": v(-24.87, 0.57) * mm, "end": v(-24.1, -0.59) * mm});
            skLineSegment(sketch, "E294.MirrorCS", {"start": v(-24.1, -0.59) * mm, "end": v(-24.65, -6.7) * mm});
            skArc(sketch, "E295.MirrorCS", {"start": v(-24.65, -6.7) * mm, "mid": v(-24.8, -7.05) * mm, "end": v(-25.12, -7.24) * mm});
            skLineSegment(sketch, "E296.MirrorCS", {"start": v(-25.12, -7.24) * mm, "end": v(-26.12, -7.47) * mm});
            skArc(sketch, "E297.MirrorCS", {"start": v(-26.12, -7.47) * mm, "mid": v(-26.5, -7.43) * mm, "end": v(-26.77, -7.18) * mm});
            skArc(sketch, "E298.MirrorCS", {"start": v(-18.08, -4.37) * mm, "mid": v(-18.17, -4.74) * mm, "end": v(-18.46, -4.98) * mm});
            skLineSegment(sketch, "E299.MirrorCS", {"start": v(-18.46, -4.98) * mm, "end": v(-19.4, -5.38) * mm});
            skArc(sketch, "E300.MirrorCS", {"start": v(-19.4, -5.38) * mm, "mid": v(-19.77, -5.4) * mm, "end": v(-20.1, -5.21) * mm});
            skLineSegment(sketch, "E301.MirrorCS", {"start": v(-20.1, -5.21) * mm, "end": v(-24.1, -0.57) * mm});
            skLineSegment(sketch, "E302.MirrorCS", {"start": v(-18.6, 1.75) * mm, "end": v(-18.08, -4.37) * mm});
            skLineSegment(sketch, "E303.MirrorCS", {"start": v(-19.57, 2.76) * mm, "end": v(-18.6, 1.75) * mm});
            skLineSegment(sketch, "E304.MirrorCS", {"start": v(-24.1, -0.57) * mm, "end": v(-24.15, 0.83) * mm});
            skLineSegment(sketch, "E305.MirrorCS", {"start": v(-24.15, 0.83) * mm, "end": v(-19.57, 2.76) * mm});
            skLineSegment(sketch, "E306.MirrorCS", {"start": v(-12.5, -1.86) * mm, "end": v(-13.37, -2.36) * mm});
            skArc(sketch, "E307.MirrorCS", {"start": v(-13.37, -2.36) * mm, "mid": v(-13.74, -2.44) * mm, "end": v(-14.08, -2.29) * mm});
            skArc(sketch, "E308.MirrorCS", {"start": v(-12.2, -1.2) * mm, "mid": v(-12.24, -1.58) * mm, "end": v(-12.5, -1.86) * mm});
            skLineSegment(sketch, "E309.MirrorCS", {"start": v(-14.08, -2.29) * mm, "end": v(-18.64, 1.83) * mm});
            skLineSegment(sketch, "E310.MirrorCS", {"start": v(-13.46, 4.8) * mm, "end": v(-12.2, -1.2) * mm});
            skLineSegment(sketch, "E311.MirrorCS", {"start": v(-18.64, 1.83) * mm, "end": v(-18.85, 3.2) * mm});
            skLineSegment(sketch, "E312.MirrorCS", {"start": v(-14.55, 5.69) * mm, "end": v(-13.46, 4.8) * mm});
            skLineSegment(sketch, "E313.MirrorCS", {"start": v(-18.85, 3.2) * mm, "end": v(-14.55, 5.69) * mm});
            skArc(sketch, "E314.MirrorCS", {"start": v(-6.61, 3.03) * mm, "mid": v(-6.58, 2.66) * mm, "end": v(-6.78, 2.34) * mm});
            skArc(sketch, "E315.MirrorCS", {"start": v(-7.56, 1.68) * mm, "mid": v(-7.91, 1.54) * mm, "end": v(-8.28, 1.63) * mm});
            skLineSegment(sketch, "E316.MirrorCS", {"start": v(-6.78, 2.34) * mm, "end": v(-7.56, 1.68) * mm});
            skLineSegment(sketch, "E317.MirrorCS", {"start": v(-8.28, 1.63) * mm, "end": v(-13.48, 4.89) * mm});
            skLineSegment(sketch, "E318.MirrorCS", {"start": v(-8.9, 8.72) * mm, "end": v(-6.61, 3.03) * mm});
            skLineSegment(sketch, "E319.MirrorCS", {"start": v(-13.48, 4.89) * mm, "end": v(-13.94, 6.2) * mm});
            skLineSegment(sketch, "E320.MirrorCS", {"start": v(-10.13, 9.4) * mm, "end": v(-8.9, 8.72) * mm});
            skLineSegment(sketch, "E321.MirrorCS", {"start": v(-13.94, 6.2) * mm, "end": v(-10.13, 9.4) * mm});
            skLineSegment(sketch, "E322.MirrorCS", {"start": v(-5.08, 13.3) * mm, "end": v(-1.83, 8.1) * mm});
            skLineSegment(sketch, "E323.MirrorCS", {"start": v(-3.23, 6.42) * mm, "end": v(-8.92, 8.72) * mm});
            skArc(sketch, "E324.MirrorCS", {"start": v(-2.53, 6.6) * mm, "mid": v(-2.85, 6.4) * mm, "end": v(-3.23, 6.42) * mm});
            skArc(sketch, "E325.MirrorCS", {"start": v(-1.83, 8.1) * mm, "mid": v(-1.74, 7.73) * mm, "end": v(-1.88, 7.38) * mm});
            skLineSegment(sketch, "E326.MirrorCS", {"start": v(-1.88, 7.38) * mm, "end": v(-2.53, 6.6) * mm});
            skLineSegment(sketch, "E327.MirrorCS", {"start": v(-8.92, 8.72) * mm, "end": v(-9.6, 9.95) * mm});
            skLineSegment(sketch, "E328.MirrorCS", {"start": v(-6.4, 13.75) * mm, "end": v(-5.08, 13.3) * mm});
            skLineSegment(sketch, "E329.MirrorCS", {"start": v(-9.6, 9.95) * mm, "end": v(-6.4, 13.75) * mm});
            skLineSegment(sketch, "E330.MirrorCS", {"start": v(2.24, 35.65) * mm, "end": v(7.88, 33.2) * mm});
            skLineSegment(sketch, "E331.MirrorCS", {"start": v(7.67, 31.04) * mm, "end": v(1.68, 29.7) * mm});
            skArc(sketch, "E332.MirrorCS", {"start": v(8.15, 31.58) * mm, "mid": v(8, 31.23) * mm, "end": v(7.67, 31.04) * mm});
            skArc(sketch, "E333.MirrorCS", {"start": v(7.88, 33.2) * mm, "mid": v(8.16, 32.96) * mm, "end": v(8.24, 32.6) * mm});
            skLineSegment(sketch, "E334.MirrorCS", {"start": v(8.24, 32.6) * mm, "end": v(8.15, 31.58) * mm});
            skLineSegment(sketch, "E335.MirrorCS", {"start": v(0.9, 35.27) * mm, "end": v(2.24, 35.65) * mm});
            skLineSegment(sketch, "E336.MirrorCS", {"start": v(1.68, 29.7) * mm, "end": v(0.43, 30.32) * mm});
            skLineSegment(sketch, "E337.MirrorCS", {"start": v(0.43, 30.32) * mm, "end": v(0.9, 35.27) * mm});
            skLineSegment(sketch, "E338.MirrorCS", {"start": v(0.36, 29.5) * mm, "end": v(1.74, 29.7) * mm});
            skLineSegment(sketch, "E339.MirrorCS", {"start": v(-0.73, 24.65) * mm, "end": v(0.36, 29.5) * mm});
            skLineSegment(sketch, "E340.MirrorCS", {"start": v(0.43, 23.88) * mm, "end": v(-0.73, 24.65) * mm});
            skLineSegment(sketch, "E341.MirrorCS", {"start": v(6.54, 24.44) * mm, "end": v(0.43, 23.88) * mm});
            skLineSegment(sketch, "E342.MirrorCS", {"start": v(1.74, 29.7) * mm, "end": v(7.02, 26.56) * mm});
            skArc(sketch, "E343.MirrorCS", {"start": v(7.08, 24.91) * mm, "mid": v(6.89, 24.6) * mm, "end": v(6.54, 24.44) * mm});
            skArc(sketch, "E344.MirrorCS", {"start": v(7.02, 26.56) * mm, "mid": v(7.27, 26.28) * mm, "end": v(7.3, 25.9) * mm});
            skLineSegment(sketch, "E345.MirrorCS", {"start": v(7.3, 25.9) * mm, "end": v(7.08, 24.91) * mm});
            skLineSegment(sketch, "E346.MirrorCS", {"start": v(4.18, 17.86) * mm, "end": v(-1.94, 18.37) * mm});
            skLineSegment(sketch, "E347.MirrorCS", {"start": v(0.37, 23.88) * mm, "end": v(5.02, 19.87) * mm});
            skArc(sketch, "E348.MirrorCS", {"start": v(5.02, 19.87) * mm, "mid": v(5.22, 19.55) * mm, "end": v(5.18, 19.17) * mm});
            skArc(sketch, "E349.MirrorCS", {"start": v(4.8, 18.23) * mm, "mid": v(4.54, 17.95) * mm, "end": v(4.18, 17.86) * mm});
            skLineSegment(sketch, "E350.MirrorCS", {"start": v(5.18, 19.17) * mm, "end": v(4.8, 18.23) * mm});
            skLineSegment(sketch, "E351.MirrorCS", {"start": v(-1.94, 18.37) * mm, "end": v(-2.95, 19.34) * mm});
            skLineSegment(sketch, "E352.MirrorCS", {"start": v(-1.02, 23.92) * mm, "end": v(0.37, 23.88) * mm});
            skLineSegment(sketch, "E353.MirrorCS", {"start": v(-2.95, 19.34) * mm, "end": v(-1.02, 23.92) * mm});
            skLineSegment(sketch, "E354.MirrorCS", {"start": v(-1.92, 18.34) * mm, "end": v(2, 13.62) * mm});
            skLineSegment(sketch, "E355.MirrorCS", {"start": v(0.83, 11.78) * mm, "end": v(-5.11, 13.3) * mm});
            skArc(sketch, "E356.MirrorCS", {"start": v(1.5, 12.05) * mm, "mid": v(1.21, 11.8) * mm, "end": v(0.83, 11.78) * mm});
            skArc(sketch, "E357.MirrorCS", {"start": v(2, 13.62) * mm, "mid": v(2.14, 13.27) * mm, "end": v(2.04, 12.9) * mm});
            skLineSegment(sketch, "E358.MirrorCS", {"start": v(2.04, 12.9) * mm, "end": v(1.5, 12.05) * mm});
            skLineSegment(sketch, "E359.MirrorCS", {"start": v(-5.11, 13.3) * mm, "end": v(-5.95, 14.42) * mm});
            skLineSegment(sketch, "E360.MirrorCS", {"start": v(-3.3, 18.62) * mm, "end": v(-1.92, 18.34) * mm});
            skLineSegment(sketch, "E361.MirrorCS", {"start": v(-5.95, 14.42) * mm, "end": v(-3.3, 18.62) * mm});
            skLineSegment(sketch, "E362", {"start": v(40.47, -45.22) * mm, "end": v(34.69, -27.42) * mm});
            skLineSegment(sketch, "E363", {"start": v(40.47, -45.22) * mm, "end": v(46.25, -27.42) * mm});
            skLineSegment(sketch, "E364", {"start": v(40.47, -45.22) * mm, "end": v(55.6, -34.22) * mm});
            skLineSegment(sketch, "E365", {"start": v(40.47, -45.22) * mm, "end": v(55.6, -56.21) * mm});
            skLineSegment(sketch, "E366", {"start": v(40.47, -45.22) * mm, "end": v(46.25, -63.01) * mm});
            skLineSegment(sketch, "E367", {"start": v(40.47, -45.22) * mm, "end": v(34.69, -63.01) * mm});
            skLineSegment(sketch, "E368", {"start": v(40.47, -45.22) * mm, "end": v(25.33, -34.22) * mm});
            skLineSegment(sketch, "E369", {"start": v(40.47, -45.22) * mm, "end": v(25.33, -56.21) * mm});
            skLineSegment(sketch, "E370", {"start": v(21.76, -45.22) * mm, "end": v(59.18, -45.22) * mm});
            skLineSegment(sketch, "E371", {"start": v(37.64, -26.65) * mm, "end": v(38.1, -27.98) * mm});
            skLineSegment(sketch, "E372", {"start": v(38.1, -27.98) * mm, "end": v(43.05, -28.18) * mm});
            skLineSegment(sketch, "E373", {"start": v(43.05, -28.18) * mm, "end": v(43.6, -26.9) * mm});
            skLineSegment(sketch, "E374", {"start": v(43.6, -26.9) * mm, "end": v(41.96, -21) * mm});
            skLineSegment(sketch, "E375", {"start": v(41.4, -20.55) * mm, "end": v(40.38, -20.5) * mm});
            skLineSegment(sketch, "E376", {"start": v(39.78, -20.9) * mm, "end": v(37.64, -26.65) * mm});
            skPoint(sketch, "E377.visualSharp", {"position": v(39.94, -20.48) * mm});
            skArc(sketch, "E377.filletArc", {"start": v(40.38, -20.5) * mm, "mid": v(40.02, -20.6) * mm, "end": v(39.78, -20.9) * mm});
            skPoint(sketch, "E378.visualSharp", {"position": v(41.84, -20.56) * mm});
            skArc(sketch, "E378.filletArc", {"start": v(41.96, -21) * mm, "mid": v(41.75, -20.68) * mm, "end": v(41.4, -20.55) * mm});
            skLineSegment(sketch, "E379", {"start": v(48.86, -28.57) * mm, "end": v(48.52, -29.93) * mm});
            skLineSegment(sketch, "E380", {"start": v(48.52, -29.93) * mm, "end": v(52.59, -32.78) * mm});
            skLineSegment(sketch, "E381", {"start": v(52.59, -32.78) * mm, "end": v(53.75, -32) * mm});
            skLineSegment(sketch, "E382", {"start": v(53.75, -32) * mm, "end": v(55.54, -26.12) * mm});
            skLineSegment(sketch, "E383", {"start": v(55.3, -25.45) * mm, "end": v(54.48, -24.86) * mm});
            skLineSegment(sketch, "E384", {"start": v(53.76, -24.88) * mm, "end": v(48.86, -28.57) * mm});
            skPoint(sketch, "E385.visualSharp", {"position": v(54.11, -24.61) * mm});
            skArc(sketch, "E385.filletArc", {"start": v(54.48, -24.86) * mm, "mid": v(54.12, -24.75) * mm, "end": v(53.76, -24.88) * mm});
            skPoint(sketch, "E386.visualSharp", {"position": v(55.67, -25.7) * mm});
            skArc(sketch, "E386.filletArc", {"start": v(55.54, -26.12) * mm, "mid": v(55.54, -25.75) * mm, "end": v(55.3, -25.45) * mm});
            skLineSegment(sketch, "E387", {"start": v(56.9, -36.63) * mm, "end": v(55.85, -37.55) * mm});
            skLineSegment(sketch, "E388", {"start": v(55.85, -37.55) * mm, "end": v(57.55, -42.22) * mm});
            skLineSegment(sketch, "E389", {"start": v(57.55, -42.22) * mm, "end": v(58.95, -42.24) * mm});
            skLineSegment(sketch, "E390", {"start": v(58.95, -42.24) * mm, "end": v(63.79, -38.47) * mm});
            skLineSegment(sketch, "E391", {"start": v(63.98, -37.78) * mm, "end": v(63.64, -36.82) * mm});
            skLineSegment(sketch, "E392", {"start": v(63.04, -36.42) * mm, "end": v(56.9, -36.63) * mm});
            skPoint(sketch, "E393.visualSharp", {"position": v(63.49, -36.4) * mm});
            skArc(sketch, "E393.filletArc", {"start": v(63.64, -36.82) * mm, "mid": v(63.4, -36.52) * mm, "end": v(63.04, -36.42) * mm});
            skPoint(sketch, "E394.visualSharp", {"position": v(64.14, -38.2) * mm});
            skArc(sketch, "E394.filletArc", {"start": v(63.79, -38.47) * mm, "mid": v(64, -38.15) * mm, "end": v(63.98, -37.78) * mm});
            skLineSegment(sketch, "E395", {"start": v(27.3, -31.87) * mm, "end": v(28.46, -32.65) * mm});
            skLineSegment(sketch, "E396", {"start": v(28.46, -32.65) * mm, "end": v(32.53, -29.8) * mm});
            skLineSegment(sketch, "E397", {"start": v(32.53, -29.8) * mm, "end": v(32.19, -28.44) * mm});
            skLineSegment(sketch, "E398", {"start": v(32.19, -28.44) * mm, "end": v(27.29, -24.75) * mm});
            skLineSegment(sketch, "E399", {"start": v(26.57, -24.74) * mm, "end": v(25.74, -25.32) * mm});
            skLineSegment(sketch, "E400", {"start": v(25.5, -26) * mm, "end": v(27.3, -31.87) * mm});
            skPoint(sketch, "E401.visualSharp", {"position": v(25.38, -25.57) * mm});
            skArc(sketch, "E401.filletArc", {"start": v(25.74, -25.32) * mm, "mid": v(25.51, -25.62) * mm, "end": v(25.5, -26) * mm});
            skPoint(sketch, "E402.visualSharp", {"position": v(26.93, -24.48) * mm});
            skArc(sketch, "E402.filletArc", {"start": v(27.29, -24.75) * mm, "mid": v(26.93, -24.63) * mm, "end": v(26.57, -24.74) * mm});
            skLineSegment(sketch, "E403", {"start": v(21.94, -42.32) * mm, "end": v(23.33, -42.25) * mm});
            skLineSegment(sketch, "E404", {"start": v(23.33, -42.25) * mm, "end": v(24.86, -37.52) * mm});
            skLineSegment(sketch, "E405", {"start": v(24.86, -37.52) * mm, "end": v(23.77, -36.64) * mm});
            skLineSegment(sketch, "E406", {"start": v(23.77, -36.64) * mm, "end": v(17.63, -36.65) * mm});
            skLineSegment(sketch, "E407", {"start": v(17.06, -37.08) * mm, "end": v(16.74, -38.04) * mm});
            skLineSegment(sketch, "E408", {"start": v(16.97, -38.72) * mm, "end": v(21.94, -42.32) * mm});
            skPoint(sketch, "E409.visualSharp", {"position": v(16.6, -38.46) * mm});
            skArc(sketch, "E409.filletArc", {"start": v(16.74, -38.04) * mm, "mid": v(16.74, -38.42) * mm, "end": v(16.97, -38.72) * mm});
            skPoint(sketch, "E410.visualSharp", {"position": v(17.2, -36.65) * mm});
            skArc(sketch, "E410.filletArc", {"start": v(17.63, -36.65) * mm, "mid": v(17.28, -36.77) * mm, "end": v(17.06, -37.08) * mm});
            skArc(sketch, "E411.MirrorCS", {"start": v(16.74, -52.39) * mm, "mid": v(16.74, -52.01) * mm, "end": v(16.97, -51.7) * mm});
            skLineSegment(sketch, "E412.MirrorCS", {"start": v(17.06, -53.35) * mm, "end": v(16.74, -52.39) * mm});
            skArc(sketch, "E413.MirrorCS", {"start": v(17.63, -53.78) * mm, "mid": v(17.28, -53.66) * mm, "end": v(17.06, -53.35) * mm});
            skLineSegment(sketch, "E414.MirrorCS", {"start": v(23.77, -53.79) * mm, "end": v(17.63, -53.78) * mm});
            skLineSegment(sketch, "E415.MirrorCS", {"start": v(16.97, -51.7) * mm, "end": v(21.94, -48.1) * mm});
            skLineSegment(sketch, "E416.MirrorCS", {"start": v(21.94, -48.1) * mm, "end": v(23.33, -48.18) * mm});
            skLineSegment(sketch, "E417.MirrorCS", {"start": v(24.86, -52.91) * mm, "end": v(23.77, -53.79) * mm});
            skLineSegment(sketch, "E418.MirrorCS", {"start": v(23.33, -48.18) * mm, "end": v(24.86, -52.91) * mm});
            skLineSegment(sketch, "E419.MirrorCS", {"start": v(25.5, -64.43) * mm, "end": v(27.3, -58.56) * mm});
            skLineSegment(sketch, "E420.MirrorCS", {"start": v(32.19, -61.99) * mm, "end": v(27.29, -65.68) * mm});
            skArc(sketch, "E421.MirrorCS", {"start": v(27.29, -65.68) * mm, "mid": v(26.93, -65.8) * mm, "end": v(26.57, -65.7) * mm});
            skArc(sketch, "E422.MirrorCS", {"start": v(25.74, -65.11) * mm, "mid": v(25.51, -64.8) * mm, "end": v(25.5, -64.43) * mm});
            skLineSegment(sketch, "E423.MirrorCS", {"start": v(26.57, -65.7) * mm, "end": v(25.74, -65.11) * mm});
            skLineSegment(sketch, "E424.MirrorCS", {"start": v(27.3, -58.56) * mm, "end": v(28.46, -57.78) * mm});
            skLineSegment(sketch, "E425.MirrorCS", {"start": v(32.53, -60.63) * mm, "end": v(32.19, -61.99) * mm});
            skLineSegment(sketch, "E426.MirrorCS", {"start": v(28.46, -57.78) * mm, "end": v(32.53, -60.63) * mm});
            skLineSegment(sketch, "E427.MirrorCS", {"start": v(39.78, -69.53) * mm, "end": v(37.64, -63.78) * mm});
            skLineSegment(sketch, "E428.MirrorCS", {"start": v(37.64, -63.78) * mm, "end": v(38.1, -62.45) * mm});
            skLineSegment(sketch, "E429.MirrorCS", {"start": v(38.1, -62.45) * mm, "end": v(43.05, -62.25) * mm});
            skLineSegment(sketch, "E430.MirrorCS", {"start": v(43.05, -62.25) * mm, "end": v(43.6, -63.53) * mm});
            skLineSegment(sketch, "E431.MirrorCS", {"start": v(43.6, -63.53) * mm, "end": v(41.96, -69.44) * mm});
            skArc(sketch, "E432.MirrorCS", {"start": v(41.96, -69.44) * mm, "mid": v(41.75, -69.75) * mm, "end": v(41.4, -69.88) * mm});
            skLineSegment(sketch, "E433.MirrorCS", {"start": v(41.4, -69.88) * mm, "end": v(40.38, -69.93) * mm});
            skArc(sketch, "E434.MirrorCS", {"start": v(40.38, -69.93) * mm, "mid": v(40.02, -69.83) * mm, "end": v(39.78, -69.53) * mm});
            skArc(sketch, "E435.MirrorCS", {"start": v(54.48, -65.57) * mm, "mid": v(54.12, -65.68) * mm, "end": v(53.76, -65.55) * mm});
            skLineSegment(sketch, "E436.MirrorCS", {"start": v(55.3, -64.98) * mm, "end": v(54.48, -65.57) * mm});
            skArc(sketch, "E437.MirrorCS", {"start": v(55.54, -64.3) * mm, "mid": v(55.54, -64.68) * mm, "end": v(55.3, -64.98) * mm});
            skLineSegment(sketch, "E438.MirrorCS", {"start": v(53.76, -65.55) * mm, "end": v(48.86, -61.86) * mm});
            skLineSegment(sketch, "E439.MirrorCS", {"start": v(53.75, -58.44) * mm, "end": v(55.54, -64.3) * mm});
            skLineSegment(sketch, "E440.MirrorCS", {"start": v(52.59, -57.65) * mm, "end": v(53.75, -58.44) * mm});
            skLineSegment(sketch, "E441.MirrorCS", {"start": v(48.52, -60.5) * mm, "end": v(52.59, -57.65) * mm});
            skLineSegment(sketch, "E442.MirrorCS", {"start": v(48.86, -61.86) * mm, "end": v(48.52, -60.5) * mm});
            skLineSegment(sketch, "E443.MirrorCS", {"start": v(63.04, -54) * mm, "end": v(56.9, -53.8) * mm});
            skLineSegment(sketch, "E444.MirrorCS", {"start": v(58.95, -48.19) * mm, "end": v(63.79, -51.97) * mm});
            skArc(sketch, "E445.MirrorCS", {"start": v(63.64, -53.6) * mm, "mid": v(63.4, -53.9) * mm, "end": v(63.04, -54) * mm});
            skArc(sketch, "E446.MirrorCS", {"start": v(63.79, -51.97) * mm, "mid": v(64, -52.28) * mm, "end": v(63.98, -52.65) * mm});
            skLineSegment(sketch, "E447.MirrorCS", {"start": v(63.98, -52.65) * mm, "end": v(63.64, -53.6) * mm});
            skLineSegment(sketch, "E448.MirrorCS", {"start": v(56.9, -53.8) * mm, "end": v(55.85, -52.88) * mm});
            skLineSegment(sketch, "E449.MirrorCS", {"start": v(55.85, -52.88) * mm, "end": v(57.55, -48.21) * mm});
            skLineSegment(sketch, "E450.MirrorCS", {"start": v(57.55, -48.21) * mm, "end": v(58.95, -48.19) * mm});
            skLineSegment(sketch, "E451", {"start": v(32.02, -28.28) * mm, "end": v(32.84, -29.41) * mm});
            skLineSegment(sketch, "E452", {"start": v(32.84, -29.41) * mm, "end": v(37.64, -28.14) * mm});
            skLineSegment(sketch, "E453", {"start": v(37.64, -28.14) * mm, "end": v(37.79, -26.75) * mm});
            skLineSegment(sketch, "E454", {"start": v(37.79, -26.75) * mm, "end": v(34.46, -21.6) * mm});
            skLineSegment(sketch, "E455", {"start": v(33.8, -21.34) * mm, "end": v(32.81, -21.6) * mm});
            skLineSegment(sketch, "E456", {"start": v(32.36, -22.15) * mm, "end": v(32.02, -28.28) * mm});
            skPoint(sketch, "E457.visualSharp", {"position": v(32.38, -21.71) * mm});
            skArc(sketch, "E457.filletArc", {"start": v(32.81, -21.6) * mm, "mid": v(32.5, -21.8) * mm, "end": v(32.36, -22.15) * mm});
            skPoint(sketch, "E458.visualSharp", {"position": v(34.22, -21.22) * mm});
            skArc(sketch, "E458.filletArc", {"start": v(34.46, -21.6) * mm, "mid": v(34.17, -21.36) * mm, "end": v(33.8, -21.34) * mm});
            skLineSegment(sketch, "E459", {"start": v(23.63, -36.5) * mm, "end": v(24.97, -36.88) * mm});
            skLineSegment(sketch, "E460", {"start": v(24.97, -36.88) * mm, "end": v(27.98, -32.93) * mm});
            skLineSegment(sketch, "E461", {"start": v(27.98, -32.93) * mm, "end": v(27.24, -31.74) * mm});
            skLineSegment(sketch, "E462", {"start": v(27.24, -31.74) * mm, "end": v(21.45, -29.72) * mm});
            skLineSegment(sketch, "E463", {"start": v(20.76, -29.92) * mm, "end": v(20.15, -30.73) * mm});
            skLineSegment(sketch, "E464", {"start": v(20.13, -31.45) * mm, "end": v(23.63, -36.5) * mm});
            skPoint(sketch, "E465.visualSharp", {"position": v(19.88, -31.08) * mm});
            skArc(sketch, "E465.filletArc", {"start": v(20.15, -30.73) * mm, "mid": v(20.02, -31.09) * mm, "end": v(20.13, -31.45) * mm});
            skPoint(sketch, "E466.visualSharp", {"position": v(21.03, -29.57) * mm});
            skArc(sketch, "E466.filletArc", {"start": v(21.45, -29.72) * mm, "mid": v(21.07, -29.7) * mm, "end": v(20.76, -29.92) * mm});
            skLineSegment(sketch, "E467", {"start": v(43.42, -26.65) * mm, "end": v(43.44, -28.05) * mm});
            skLineSegment(sketch, "E468", {"start": v(43.44, -28.05) * mm, "end": v(48.1, -29.77) * mm});
            skLineSegment(sketch, "E469", {"start": v(48.1, -29.77) * mm, "end": v(49.02, -28.72) * mm});
            skLineSegment(sketch, "E470", {"start": v(49.02, -28.72) * mm, "end": v(49.27, -22.6) * mm});
            skLineSegment(sketch, "E471", {"start": v(48.87, -22) * mm, "end": v(47.92, -21.64) * mm});
            skLineSegment(sketch, "E472", {"start": v(47.23, -21.84) * mm, "end": v(43.42, -26.65) * mm});
            skPoint(sketch, "E473.visualSharp", {"position": v(47.5, -21.49) * mm});
            skArc(sketch, "E473.filletArc", {"start": v(47.92, -21.64) * mm, "mid": v(47.54, -21.63) * mm, "end": v(47.23, -21.84) * mm});
            skPoint(sketch, "E474.visualSharp", {"position": v(49.29, -22.15) * mm});
            skArc(sketch, "E474.filletArc", {"start": v(49.27, -22.6) * mm, "mid": v(49.17, -22.23) * mm, "end": v(48.87, -22) * mm});
            skLineSegment(sketch, "E475", {"start": v(53.6, -32.02) * mm, "end": v(52.88, -33.2) * mm});
            skLineSegment(sketch, "E476", {"start": v(52.88, -33.2) * mm, "end": v(55.91, -37.14) * mm});
            skLineSegment(sketch, "E477", {"start": v(55.91, -37.14) * mm, "end": v(57.25, -36.74) * mm});
            skLineSegment(sketch, "E478", {"start": v(57.25, -36.74) * mm, "end": v(60.72, -31.68) * mm});
            skLineSegment(sketch, "E479", {"start": v(60.7, -30.96) * mm, "end": v(60.08, -30.16) * mm});
            skLineSegment(sketch, "E480", {"start": v(59.4, -29.96) * mm, "end": v(53.6, -32.02) * mm});
            skPoint(sketch, "E481.visualSharp", {"position": v(59.8, -29.8) * mm});
            skArc(sketch, "E481.filletArc", {"start": v(60.08, -30.16) * mm, "mid": v(59.77, -29.95) * mm, "end": v(59.4, -29.96) * mm});
            skPoint(sketch, "E482.visualSharp", {"position": v(60.97, -31.31) * mm});
            skArc(sketch, "E482.filletArc", {"start": v(60.72, -31.68) * mm, "mid": v(60.82, -31.32) * mm, "end": v(60.7, -30.96) * mm});
            skPoint(sketch, "E483.MirrorP", {"position": v(19.88, -59.35) * mm});
            skArc(sketch, "E484.MirrorCS", {"start": v(20.15, -59.7) * mm, "mid": v(20.02, -59.34) * mm, "end": v(20.13, -58.98) * mm});
            skLineSegment(sketch, "E485.MirrorCS", {"start": v(20.76, -60.5) * mm, "end": v(20.15, -59.7) * mm});
            skPoint(sketch, "E486.MirrorP", {"position": v(21.03, -60.86) * mm});
            skArc(sketch, "E487.MirrorCS", {"start": v(21.45, -60.71) * mm, "mid": v(21.07, -60.72) * mm, "end": v(20.76, -60.5) * mm});
            skLineSegment(sketch, "E488.MirrorCS", {"start": v(27.24, -58.7) * mm, "end": v(21.45, -60.71) * mm});
            skLineSegment(sketch, "E489.MirrorCS", {"start": v(20.13, -58.98) * mm, "end": v(23.63, -53.94) * mm});
            skLineSegment(sketch, "E490.MirrorCS", {"start": v(24.97, -53.55) * mm, "end": v(27.98, -57.5) * mm});
            skLineSegment(sketch, "E491.MirrorCS", {"start": v(27.98, -57.5) * mm, "end": v(27.24, -58.7) * mm});
            skLineSegment(sketch, "E492.MirrorCS", {"start": v(23.63, -53.94) * mm, "end": v(24.97, -53.55) * mm});
            skLineSegment(sketch, "E493.MirrorCS", {"start": v(32.36, -68.28) * mm, "end": v(32.02, -62.15) * mm});
            skLineSegment(sketch, "E494.MirrorCS", {"start": v(33.8, -69.1) * mm, "end": v(32.81, -68.83) * mm});
            skArc(sketch, "E495.MirrorCS", {"start": v(32.81, -68.83) * mm, "mid": v(32.5, -68.63) * mm, "end": v(32.36, -68.28) * mm});
            skArc(sketch, "E496.MirrorCS", {"start": v(34.46, -68.83) * mm, "mid": v(34.17, -69.07) * mm, "end": v(33.8, -69.1) * mm});
            skLineSegment(sketch, "E497.MirrorCS", {"start": v(37.79, -63.68) * mm, "end": v(34.46, -68.83) * mm});
            skLineSegment(sketch, "E498.MirrorCS", {"start": v(37.64, -62.29) * mm, "end": v(37.79, -63.68) * mm});
            skLineSegment(sketch, "E499.MirrorCS", {"start": v(32.84, -61.02) * mm, "end": v(37.64, -62.29) * mm});
            skLineSegment(sketch, "E500.MirrorCS", {"start": v(32.02, -62.15) * mm, "end": v(32.84, -61.02) * mm});
            skLineSegment(sketch, "E501.MirrorCS", {"start": v(47.23, -68.6) * mm, "end": v(43.42, -63.78) * mm});
            skLineSegment(sketch, "E502.MirrorCS", {"start": v(49.02, -61.7) * mm, "end": v(49.27, -67.84) * mm});
            skArc(sketch, "E503.MirrorCS", {"start": v(49.27, -67.84) * mm, "mid": v(49.17, -68.2) * mm, "end": v(48.87, -68.44) * mm});
            skArc(sketch, "E504.MirrorCS", {"start": v(47.92, -68.79) * mm, "mid": v(47.54, -68.8) * mm, "end": v(47.23, -68.6) * mm});
            skLineSegment(sketch, "E505.MirrorCS", {"start": v(48.87, -68.44) * mm, "end": v(47.92, -68.79) * mm});
            skLineSegment(sketch, "E506.MirrorCS", {"start": v(43.42, -63.78) * mm, "end": v(43.44, -62.38) * mm});
            skLineSegment(sketch, "E507.MirrorCS", {"start": v(43.44, -62.38) * mm, "end": v(48.1, -60.66) * mm});
            skLineSegment(sketch, "E508.MirrorCS", {"start": v(48.1, -60.66) * mm, "end": v(49.02, -61.7) * mm});
            skLineSegment(sketch, "E509.MirrorCS", {"start": v(57.25, -53.69) * mm, "end": v(60.72, -58.75) * mm});
            skLineSegment(sketch, "E510.MirrorCS", {"start": v(59.4, -60.47) * mm, "end": v(53.6, -58.41) * mm});
            skLineSegment(sketch, "E511.MirrorCS", {"start": v(60.7, -59.47) * mm, "end": v(60.08, -60.27) * mm});
            skArc(sketch, "E512.MirrorCS", {"start": v(60.08, -60.27) * mm, "mid": v(59.77, -60.48) * mm, "end": v(59.4, -60.47) * mm});
            skArc(sketch, "E513.MirrorCS", {"start": v(60.72, -58.75) * mm, "mid": v(60.82, -59.11) * mm, "end": v(60.7, -59.47) * mm});
            skLineSegment(sketch, "E514.MirrorCS", {"start": v(53.6, -58.41) * mm, "end": v(52.88, -57.22) * mm});
            skLineSegment(sketch, "E515.MirrorCS", {"start": v(55.91, -53.29) * mm, "end": v(57.25, -53.69) * mm});
            skLineSegment(sketch, "E516.MirrorCS", {"start": v(52.88, -57.22) * mm, "end": v(55.91, -53.29) * mm});
            skLineSegment(sketch, "E517", {"start": v(59.13, -42.24) * mm, "end": v(57.8, -42.69) * mm});
            skLineSegment(sketch, "E518", {"start": v(57.8, -42.69) * mm, "end": v(57.6, -47.65) * mm});
            skLineSegment(sketch, "E519", {"start": v(57.6, -47.65) * mm, "end": v(58.88, -48.2) * mm});
            skLineSegment(sketch, "E520", {"start": v(58.88, -48.2) * mm, "end": v(64.79, -46.56) * mm});
            skLineSegment(sketch, "E521", {"start": v(65.23, -46) * mm, "end": v(65.28, -44.98) * mm});
            skLineSegment(sketch, "E522", {"start": v(64.88, -44.38) * mm, "end": v(59.13, -42.24) * mm});
            skPoint(sketch, "E523.visualSharp", {"position": v(65.3, -44.54) * mm});
            skArc(sketch, "E523.filletArc", {"start": v(65.28, -44.98) * mm, "mid": v(65.18, -44.62) * mm, "end": v(64.88, -44.38) * mm});
            skPoint(sketch, "E524.visualSharp", {"position": v(65.22, -46.44) * mm});
            skArc(sketch, "E524.filletArc", {"start": v(64.79, -46.56) * mm, "mid": v(65.1, -46.35) * mm, "end": v(65.23, -46) * mm});
            skLineSegment(sketch, "E525", {"start": v(40.47, -26.5) * mm, "end": v(40.47, -63.93) * mm});
            skLineSegment(sketch, "E526.MirrorCS", {"start": v(16.06, -44.38) * mm, "end": v(21.81, -42.24) * mm});
            skLineSegment(sketch, "E527.MirrorCS", {"start": v(21.81, -42.24) * mm, "end": v(23.14, -42.69) * mm});
            skLineSegment(sketch, "E528.MirrorCS", {"start": v(23.14, -42.69) * mm, "end": v(23.34, -47.65) * mm});
            skLineSegment(sketch, "E529.MirrorCS", {"start": v(23.34, -47.65) * mm, "end": v(22.06, -48.2) * mm});
            skLineSegment(sketch, "E530.MirrorCS", {"start": v(22.06, -48.2) * mm, "end": v(16.15, -46.56) * mm});
            skArc(sketch, "E531.MirrorCS", {"start": v(16.15, -46.56) * mm, "mid": v(15.84, -46.35) * mm, "end": v(15.7, -46) * mm});
            skLineSegment(sketch, "E532.MirrorCS", {"start": v(15.7, -46) * mm, "end": v(15.66, -44.98) * mm});
            skArc(sketch, "E533.MirrorCS", {"start": v(15.66, -44.98) * mm, "mid": v(15.76, -44.62) * mm, "end": v(16.06, -44.38) * mm});
            skSolve(sketch);
        }
        {
            var Q0;
            Q0=makeQuery(id+"F0.imprint","IMPRINT",FACE,{"disambiguationData":[TD([[makeQuery(id+"F0.imprint","IMPRINT",EDGE,{"derivedFrom":sQuery(id+"F0.wireOp",EDGE,"E0")}),1.0]])]});
            extrude(context, id + "F1", {"entities" : qUnion([Q0]), "depth" : 12.7 * mm});
        }
        {
            var Q0;
            Q0 = qSketchRegion(id + "F0", true);
            var Q1;
            {var subQ0=sQuery(id+"F0.wireOp",EDGE,"E396");Q1=makeQuery(id+"F0.imprint","IMPRINT",FACE,{"disambiguationData":[TD([[makeQuery(id+"F0.imprint","IMPRINT",EDGE,{"derivedFrom":subQ0}),-1.0]])]});}
            var Q2;
            {var subQ0=sQuery(id+"F0.wireOp",EDGE,"E396");Q2=makeQuery(id+"F0.imprint","IMPRINT",FACE,{"disambiguationData":[TD([[makeQuery(id+"F0.imprint","IMPRINT",EDGE,{"derivedFrom":subQ0}),1.0]])]});}
            var Q3;
            {var subQ3=sQuery(id+"F0.wireOp",EDGE,"E368");var subQ5=sQuery(id+"F0.wireOp",EDGE,"E1");var subQ6=makeQuery(id+"F0.imprint","INTERSECT",VERTEX,{"derivedFrom":[subQ5,subQ3]});Q3=makeQuery(id+"F0.imprint","IMPRINT",FACE,{"disambiguationData":[TD([[makeQuery(id+"F0.imprint","IMPRINT",EDGE,{"disambiguationData":[TD([[subQ6,1.0]])],"derivedFrom":subQ5}),1.0]])]});}
            var Q4;
            {var subQ5=sQuery(id+"F0.wireOp",EDGE,"E1");var subQ7=sQuery(id+"F0.wireOp",EDGE,"E370");var subQ9=makeQuery(id+"F0.imprint","INTERSECT",VERTEX,{"disambiguationData":[OD(0.0)],"derivedFrom":[subQ5,subQ7]});Q4=makeQuery(id+"F0.imprint","IMPRINT",FACE,{"disambiguationData":[TD([[makeQuery(id+"F0.imprint","IMPRINT",EDGE,{"disambiguationData":[TD([[subQ9,1.0]])],"derivedFrom":subQ5}),1.0]])]});}
            var Q5;
            {var subQ3=sQuery(id+"F0.wireOp",EDGE,"E370");var subQ6=sQuery(id+"F0.wireOp",EDGE,"E1");var subQ9=makeQuery(id+"F0.imprint","INTERSECT",VERTEX,{"disambiguationData":[OD(0.0)],"derivedFrom":[subQ6,subQ3]});Q5=makeQuery(id+"F0.imprint","IMPRINT",FACE,{"disambiguationData":[TD([[makeQuery(id+"F0.imprint","IMPRINT",EDGE,{"disambiguationData":[TD([[subQ9,-1.0]])],"derivedFrom":subQ6}),1.0]])]});}
            var Q6;
            {var subQ0=sQuery(id+"F0.wireOp",EDGE,"E426.MirrorCS");Q6=makeQuery(id+"F0.imprint","IMPRINT",FACE,{"disambiguationData":[TD([[makeQuery(id+"F0.imprint","IMPRINT",EDGE,{"derivedFrom":subQ0}),1.0]])]});}
            var Q7;
            {var subQ5=sQuery(id+"F0.wireOp",EDGE,"E525");var subQ6=sQuery(id+"F0.wireOp",EDGE,"E3");var subQ7=makeQuery(id+"F0.imprint","INTERSECT",VERTEX,{"disambiguationData":[OD(1.0)],"derivedFrom":[subQ6,subQ5]});Q7=makeQuery(id+"F0.imprint","IMPRINT",FACE,{"disambiguationData":[TD([[makeQuery(id+"F0.imprint","IMPRINT",EDGE,{"disambiguationData":[TD([[subQ7,-1.0]])],"derivedFrom":subQ6}),-1.0]])]});}
            var Q8;
            {var subQ5=sQuery(id+"F0.wireOp",EDGE,"E367");var subQ6=sQuery(id+"F0.wireOp",EDGE,"E3");var subQ7=makeQuery(id+"F0.imprint","INTERSECT",VERTEX,{"derivedFrom":[subQ6,subQ5]});Q8=makeQuery(id+"F0.imprint","IMPRINT",FACE,{"disambiguationData":[TD([[makeQuery(id+"F0.imprint","IMPRINT",EDGE,{"disambiguationData":[TD([[subQ7,-1.0]])],"derivedFrom":subQ6}),-1.0]])]});}
            var Q9;
            {var subQ0=sQuery(id+"F0.wireOp",EDGE,"E441.MirrorCS");Q9=makeQuery(id+"F0.imprint","IMPRINT",FACE,{"disambiguationData":[TD([[makeQuery(id+"F0.imprint","IMPRINT",EDGE,{"derivedFrom":subQ0}),1.0]])]});}
            var Q10;
            {var subQ5=sQuery(id+"F0.wireOp",EDGE,"E449.MirrorCS");Q10=makeQuery(id+"F0.imprint","IMPRINT",FACE,{"disambiguationData":[TD([[makeQuery(id+"F0.imprint","IMPRINT",EDGE,{"derivedFrom":subQ5}),1.0]])]});}
            var Q11;
            {var subQ10=sQuery(id+"F0.wireOp",EDGE,"E380");Q11=makeQuery(id+"F0.imprint","IMPRINT",FACE,{"disambiguationData":[TD([[makeQuery(id+"F0.imprint","IMPRINT",EDGE,{"derivedFrom":subQ10}),-1.0]])]});}
            var Q12;
            {var subQ5=sQuery(id+"F0.wireOp",EDGE,"E363");var subQ6=sQuery(id+"F0.wireOp",EDGE,"E3");var subQ7=makeQuery(id+"F0.imprint","INTERSECT",VERTEX,{"derivedFrom":[subQ6,subQ5]});Q12=makeQuery(id+"F0.imprint","IMPRINT",FACE,{"disambiguationData":[TD([[makeQuery(id+"F0.imprint","IMPRINT",EDGE,{"disambiguationData":[TD([[subQ7,-1.0]])],"derivedFrom":subQ6}),-1.0]])]});}
            var Q13;
            {var subQ5=sQuery(id+"F0.wireOp",EDGE,"E525");var subQ6=sQuery(id+"F0.wireOp",EDGE,"E3");var subQ7=makeQuery(id+"F0.imprint","INTERSECT",VERTEX,{"disambiguationData":[OD(0.0)],"derivedFrom":[subQ6,subQ5]});Q13=makeQuery(id+"F0.imprint","IMPRINT",FACE,{"disambiguationData":[TD([[makeQuery(id+"F0.imprint","IMPRINT",EDGE,{"disambiguationData":[TD([[subQ7,-1.0]])],"derivedFrom":subQ6}),-1.0]])]});}
            var Q14;
            {var subQ3=sQuery(id+"F0.wireOp",EDGE,"E369");var subQ6=sQuery(id+"F0.wireOp",EDGE,"E1");var subQ9=makeQuery(id+"F0.imprint","INTERSECT",VERTEX,{"derivedFrom":[subQ6,subQ3]});Q14=makeQuery(id+"F0.imprint","IMPRINT",FACE,{"disambiguationData":[TD([[makeQuery(id+"F0.imprint","IMPRINT",EDGE,{"disambiguationData":[TD([[subQ9,-1.0]])],"derivedFrom":subQ6}),1.0]])]});}
            var Q15;
            {var subQ0=sQuery(id+"F0.wireOp",EDGE,"E426.MirrorCS");Q15=makeQuery(id+"F0.imprint","IMPRINT",FACE,{"disambiguationData":[TD([[makeQuery(id+"F0.imprint","IMPRINT",EDGE,{"derivedFrom":subQ0}),-1.0]])]});}
            var Q16;
            {var subQ5=sQuery(id+"F0.wireOp",EDGE,"E1");var subQ7=sQuery(id+"F0.wireOp",EDGE,"E367");var subQ8=makeQuery(id+"F0.imprint","INTERSECT",VERTEX,{"derivedFrom":[subQ5,subQ7]});Q16=makeQuery(id+"F0.imprint","IMPRINT",FACE,{"disambiguationData":[TD([[makeQuery(id+"F0.imprint","IMPRINT",EDGE,{"disambiguationData":[TD([[subQ8,1.0]])],"derivedFrom":subQ5}),1.0]])]});}
            var Q17;
            {var subQ5=sQuery(id+"F0.wireOp",EDGE,"E1");var subQ7=sQuery(id+"F0.wireOp",EDGE,"E367");var subQ8=makeQuery(id+"F0.imprint","INTERSECT",VERTEX,{"derivedFrom":[subQ5,subQ7]});Q17=makeQuery(id+"F0.imprint","IMPRINT",FACE,{"disambiguationData":[TD([[makeQuery(id+"F0.imprint","IMPRINT",EDGE,{"disambiguationData":[TD([[subQ8,-1.0]])],"derivedFrom":subQ5}),1.0]])]});}
            var Q18;
            {var subQ3=sQuery(id+"F0.wireOp",EDGE,"E1");var subQ8=sQuery(id+"F0.wireOp",EDGE,"E525");var subQ10=makeQuery(id+"F0.imprint","INTERSECT",VERTEX,{"disambiguationData":[OD(1.0)],"derivedFrom":[subQ3,subQ8]});Q18=makeQuery(id+"F0.imprint","IMPRINT",FACE,{"disambiguationData":[TD([[makeQuery(id+"F0.imprint","IMPRINT",EDGE,{"disambiguationData":[TD([[subQ10,1.0]])],"derivedFrom":subQ3}),1.0]])]});}
            var Q19;
            {var subQ1=sQuery(id+"F0.wireOp",EDGE,"E1");var subQ7=sQuery(id+"F0.wireOp",EDGE,"E525");var subQ9=makeQuery(id+"F0.imprint","INTERSECT",VERTEX,{"disambiguationData":[OD(1.0)],"derivedFrom":[subQ1,subQ7]});Q19=makeQuery(id+"F0.imprint","IMPRINT",FACE,{"disambiguationData":[TD([[makeQuery(id+"F0.imprint","IMPRINT",EDGE,{"disambiguationData":[TD([[subQ9,-1.0]])],"derivedFrom":subQ1}),1.0]])]});}
            var Q20;
            {var subQ3=sQuery(id+"F0.wireOp",EDGE,"E1");var subQ7=sQuery(id+"F0.wireOp",EDGE,"E366");var subQ8=makeQuery(id+"F0.imprint","INTERSECT",VERTEX,{"derivedFrom":[subQ3,subQ7]});Q20=makeQuery(id+"F0.imprint","IMPRINT",FACE,{"disambiguationData":[TD([[makeQuery(id+"F0.imprint","IMPRINT",EDGE,{"disambiguationData":[TD([[subQ8,1.0]])],"derivedFrom":subQ3}),1.0]])]});}
            var Q21;
            {var subQ5=sQuery(id+"F0.wireOp",EDGE,"E1");var subQ7=sQuery(id+"F0.wireOp",EDGE,"E366");var subQ8=makeQuery(id+"F0.imprint","INTERSECT",VERTEX,{"derivedFrom":[subQ5,subQ7]});Q21=makeQuery(id+"F0.imprint","IMPRINT",FACE,{"disambiguationData":[TD([[makeQuery(id+"F0.imprint","IMPRINT",EDGE,{"disambiguationData":[TD([[subQ8,-1.0]])],"derivedFrom":subQ5}),1.0]])]});}
            var Q22;
            {var subQ0=sQuery(id+"F0.wireOp",EDGE,"E441.MirrorCS");Q22=makeQuery(id+"F0.imprint","IMPRINT",FACE,{"disambiguationData":[TD([[makeQuery(id+"F0.imprint","IMPRINT",EDGE,{"derivedFrom":subQ0}),-1.0]])]});}
            var Q23;
            {var subQ1=sQuery(id+"F0.wireOp",EDGE,"E1");var subQ5=sQuery(id+"F0.wireOp",EDGE,"E365");var subQ6=makeQuery(id+"F0.imprint","INTERSECT",VERTEX,{"derivedFrom":[subQ1,subQ5]});Q23=makeQuery(id+"F0.imprint","IMPRINT",FACE,{"disambiguationData":[TD([[makeQuery(id+"F0.imprint","IMPRINT",EDGE,{"disambiguationData":[TD([[subQ6,1.0]])],"derivedFrom":subQ1}),1.0]])]});}
            var Q24;
            {var subQ0=sQuery(id+"F0.wireOp",EDGE,"E365");var subQ1=sQuery(id+"F0.wireOp",EDGE,"E1");var subQ2=makeQuery(id+"F0.imprint","INTERSECT",VERTEX,{"derivedFrom":[subQ1,subQ0]});Q24=makeQuery(id+"F0.imprint","IMPRINT",FACE,{"disambiguationData":[TD([[makeQuery(id+"F0.imprint","IMPRINT",EDGE,{"disambiguationData":[TD([[subQ2,-1.0]])],"derivedFrom":subQ1}),1.0]])]});}
            var Q25;
            {var subQ1=sQuery(id+"F0.wireOp",EDGE,"E449.MirrorCS");Q25=makeQuery(id+"F0.imprint","IMPRINT",FACE,{"disambiguationData":[TD([[makeQuery(id+"F0.imprint","IMPRINT",EDGE,{"derivedFrom":subQ1}),-1.0]])]});}
            var Q26;
            {var subQ3=sQuery(id+"F0.wireOp",EDGE,"E370");var subQ5=sQuery(id+"F0.wireOp",EDGE,"E1");var subQ6=makeQuery(id+"F0.imprint","INTERSECT",VERTEX,{"disambiguationData":[OD(1.0)],"derivedFrom":[subQ5,subQ3]});Q26=makeQuery(id+"F0.imprint","IMPRINT",FACE,{"disambiguationData":[TD([[makeQuery(id+"F0.imprint","IMPRINT",EDGE,{"disambiguationData":[TD([[subQ6,1.0]])],"derivedFrom":subQ5}),1.0]])]});}
            var Q27;
            {var subQ5=sQuery(id+"F0.wireOp",EDGE,"E1");var subQ7=sQuery(id+"F0.wireOp",EDGE,"E364");var subQ8=makeQuery(id+"F0.imprint","INTERSECT",VERTEX,{"derivedFrom":[subQ5,subQ7]});Q27=makeQuery(id+"F0.imprint","IMPRINT",FACE,{"disambiguationData":[TD([[makeQuery(id+"F0.imprint","IMPRINT",EDGE,{"disambiguationData":[TD([[subQ8,-1.0]])],"derivedFrom":subQ5}),1.0]])]});}
            var Q28;
            {var subQ5=sQuery(id+"F0.wireOp",EDGE,"E1");var subQ9=sQuery(id+"F0.wireOp",EDGE,"E363");var subQ10=makeQuery(id+"F0.imprint","INTERSECT",VERTEX,{"derivedFrom":[subQ5,subQ9]});Q28=makeQuery(id+"F0.imprint","IMPRINT",FACE,{"disambiguationData":[TD([[makeQuery(id+"F0.imprint","IMPRINT",EDGE,{"disambiguationData":[TD([[subQ10,1.0]])],"derivedFrom":subQ5}),1.0]])]});}
            var Q29;
            {var subQ5=sQuery(id+"F0.wireOp",EDGE,"E363");var subQ6=sQuery(id+"F0.wireOp",EDGE,"E1");var subQ7=makeQuery(id+"F0.imprint","INTERSECT",VERTEX,{"derivedFrom":[subQ6,subQ5]});Q29=makeQuery(id+"F0.imprint","IMPRINT",FACE,{"disambiguationData":[TD([[makeQuery(id+"F0.imprint","IMPRINT",EDGE,{"disambiguationData":[TD([[subQ7,-1.0]])],"derivedFrom":subQ6}),1.0]])]});}
            var Q30;
            {var subQ1=sQuery(id+"F0.wireOp",EDGE,"E1");var subQ7=sQuery(id+"F0.wireOp",EDGE,"E525");var subQ9=makeQuery(id+"F0.imprint","INTERSECT",VERTEX,{"disambiguationData":[OD(0.0)],"derivedFrom":[subQ1,subQ7]});Q30=makeQuery(id+"F0.imprint","IMPRINT",FACE,{"disambiguationData":[TD([[makeQuery(id+"F0.imprint","IMPRINT",EDGE,{"disambiguationData":[TD([[subQ9,1.0]])],"derivedFrom":subQ1}),1.0]])]});}
            var Q31;
            {var subQ7=sQuery(id+"F0.wireOp",EDGE,"E525");var subQ9=sQuery(id+"F0.wireOp",EDGE,"E1");var subQ10=makeQuery(id+"F0.imprint","INTERSECT",VERTEX,{"disambiguationData":[OD(0.0)],"derivedFrom":[subQ9,subQ7]});Q31=makeQuery(id+"F0.imprint","IMPRINT",FACE,{"disambiguationData":[TD([[makeQuery(id+"F0.imprint","IMPRINT",EDGE,{"disambiguationData":[TD([[subQ10,-1.0]])],"derivedFrom":subQ9}),1.0]])]});}
            var Q32;
            {var subQ3=sQuery(id+"F0.wireOp",EDGE,"E362");var subQ5=sQuery(id+"F0.wireOp",EDGE,"E1");var subQ6=makeQuery(id+"F0.imprint","INTERSECT",VERTEX,{"derivedFrom":[subQ5,subQ3]});Q32=makeQuery(id+"F0.imprint","IMPRINT",FACE,{"disambiguationData":[TD([[makeQuery(id+"F0.imprint","IMPRINT",EDGE,{"disambiguationData":[TD([[subQ6,1.0]])],"derivedFrom":subQ5}),1.0]])]});}
            var Q33;
            {var subQ5=sQuery(id+"F0.wireOp",EDGE,"E1");var subQ7=sQuery(id+"F0.wireOp",EDGE,"E362");var subQ8=makeQuery(id+"F0.imprint","INTERSECT",VERTEX,{"derivedFrom":[subQ5,subQ7]});Q33=makeQuery(id+"F0.imprint","IMPRINT",FACE,{"disambiguationData":[TD([[makeQuery(id+"F0.imprint","IMPRINT",EDGE,{"disambiguationData":[TD([[subQ8,-1.0]])],"derivedFrom":subQ5}),1.0]])]});}
            var Q34;
            {var subQ1=sQuery(id+"F0.wireOp",EDGE,"E380");Q34=makeQuery(id+"F0.imprint","IMPRINT",FACE,{"disambiguationData":[TD([[makeQuery(id+"F0.imprint","IMPRINT",EDGE,{"derivedFrom":subQ1}),1.0]])]});}
            var Q35;
            {var subQ7=sQuery(id+"F0.wireOp",EDGE,"E1");var subQ9=sQuery(id+"F0.wireOp",EDGE,"E364");var subQ10=makeQuery(id+"F0.imprint","INTERSECT",VERTEX,{"derivedFrom":[subQ7,subQ9]});Q35=makeQuery(id+"F0.imprint","IMPRINT",FACE,{"disambiguationData":[TD([[makeQuery(id+"F0.imprint","IMPRINT",EDGE,{"disambiguationData":[TD([[subQ10,1.0]])],"derivedFrom":subQ7}),1.0]])]});}
            extrude(context, id + "F2", {"entities" : qUnion([Q0, Q1, Q2, Q3, Q4, Q5, Q6, Q7, Q8, Q9, Q10, Q11, Q12, Q13, Q14, Q15, Q16, Q17, Q18, Q19, Q20, Q21, Q22, Q23, Q24, Q25, Q26, Q27, Q28, Q29, Q30, Q31, Q32, Q33, Q34, Q35]), "operationType" : NewBodyOperationType.ADD, "depth" : 12.7 * mm});
        }
    });
